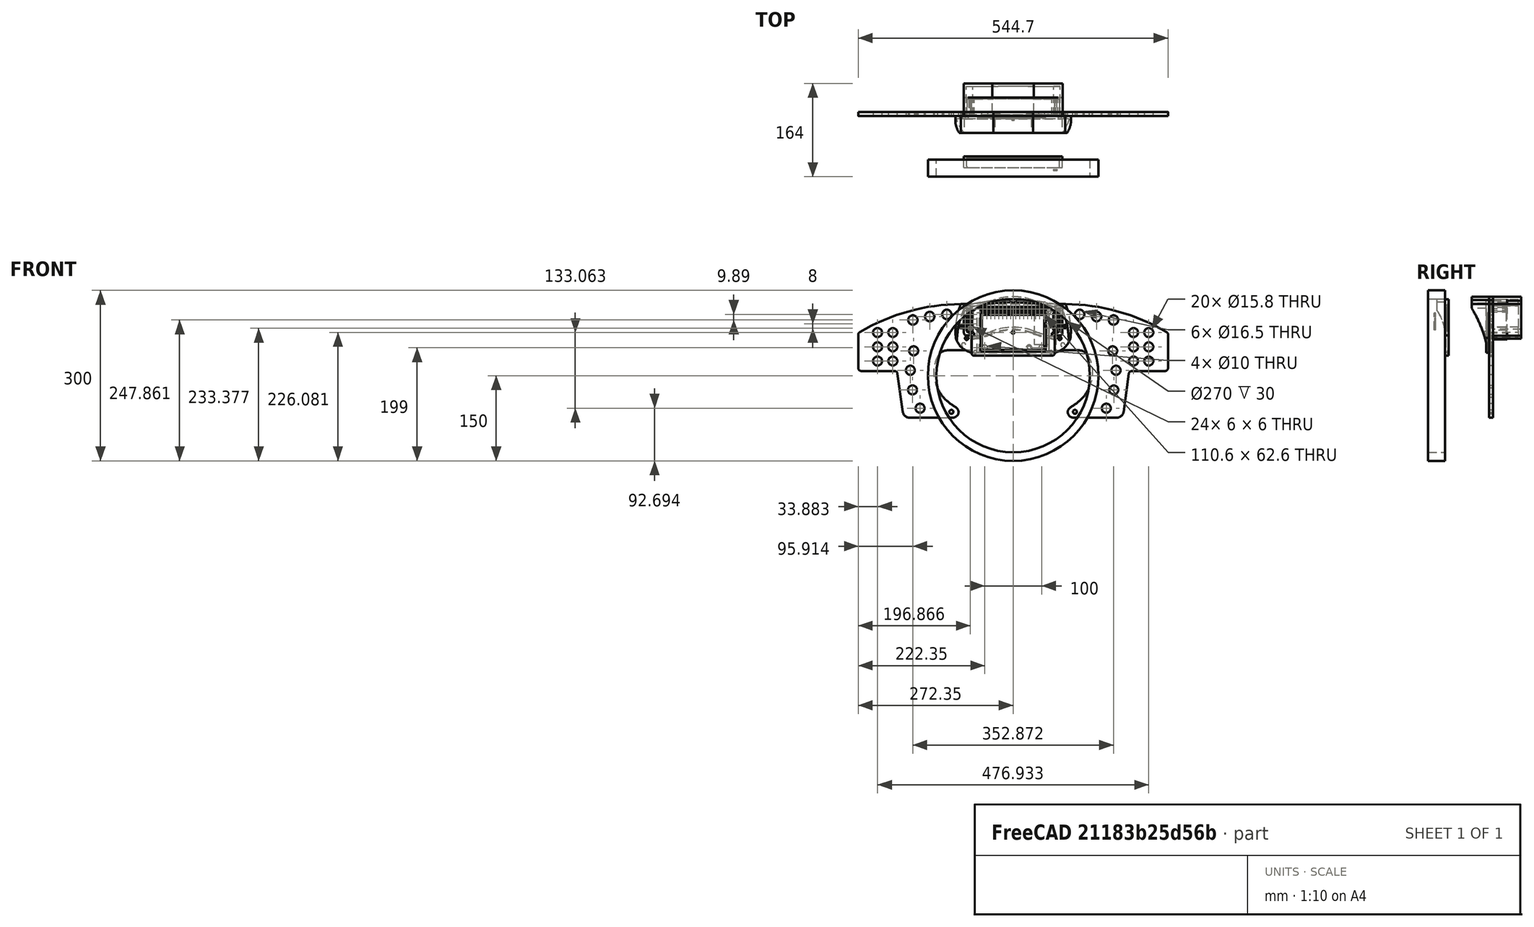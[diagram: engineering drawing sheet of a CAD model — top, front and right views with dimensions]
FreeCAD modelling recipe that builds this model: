
FCSTD DOCUMENT  (FreeCAD 0.20R29177 (Git))
Label: CSW Dashboard V1.1
License: All rights reserved
LicenseURL: http://en.wikipedia.org/wiki/All_rights_reserved
objects: Sketcher::SketchObject×51, PartDesign::Pocket×26, PartDesign::Pad×18, PartDesign::Body×9, PartDesign::Mirrored×3, PartDesign::Chamfer×2, Mesh::Feature×2, Image::ImagePlane×1, Spreadsheet::Sheet×1, Part::FeaturePython×1
note: 156 computed .brp shape members not serialized (recipe doc carries the construction recipe); baked Part::Feature solids carry a one-line shape summary decoded from their .brp

FEATURE [Image::ImagePlane] ImagePlane  label="_CSW_reference"
  Placement = pos=(1.5,53,-30.7) rot=(-1,0,0;4.71239rad)
  XSize = 323.235
  YSize = 168.408
FEATURE [Sketcher::SketchObject] Sketch  label="sk_mount_plate"
  AttachmentOffset = pos=(0,14,0) rot=(0,0,1;0rad)
  FullyConstrained = true
  MapMode = 5
  Placement = pos=(0,-3.1e-15,14) rot=(1,0,0;1.5708rad)
  Support = -> [XZ_Plane002]
  sketch-geometry (13):
    g0: Circle CenterX=-28 CenterY=0 CenterZ=0 NormalX=0 NormalY=0 NormalZ=1 AngleXU=0 Radius=2.425
    g1: Circle CenterX=28 CenterY=0 CenterZ=0 NormalX=0 NormalY=0 NormalZ=1 AngleXU=0 Radius=2.425
    g2: Circle CenterX=-50 CenterY=0 CenterZ=0 NormalX=0 NormalY=0 NormalZ=1 AngleXU=0 Radius=4.85
    g3: Circle CenterX=50 CenterY=0 CenterZ=0 NormalX=0 NormalY=0 NormalZ=1 AngleXU=0 Radius=4.85
    g4: LineSegment StartX=-50 StartY=0 StartZ=0 EndX=50 EndY=0 EndZ=0
    g5: ArcOfCircle CenterX=-5.9e-15 CenterY=-69 CenterZ=0 NormalX=0 NormalY=0 NormalZ=1 AngleXU=0 Radius=100 StartAngle=1.21654 EndAngle=1.92505
    g6: ArcOfCircle CenterX=106.026 CenterY=217.668 CenterZ=0 NormalX=0 NormalY=0 NormalZ=1 AngleXU=0 Radius=205.647 StartAngle=4.35814 EndAngle=4.64413
    g7: GeomPoint X=0 Y=31 Z=0
    g8: LineSegment StartX=28 StartY=0 StartZ=0 EndX=28 EndY=27 EndZ=0
    g9: LineSegment StartX=50 StartY=0 StartZ=0 EndX=50 EndY=19.8 EndZ=0
    g10: ArcOfCircle CenterX=-106.026 CenterY=217.668 CenterZ=0 NormalX=0 NormalY=0 NormalZ=1 AngleXU=0 Radius=205.647 StartAngle=4.78065 EndAngle=5.06664
    g11: LineSegment StartX=-50 StartY=0 StartZ=0 EndX=-50 EndY=19.8 EndZ=0
    g12: LineSegment StartX=-92 StartY=12.5 StartZ=0 EndX=-92 EndY=0 EndZ=0
  constraints (36):
    c: DistanceX(g0,g1) = 56  'mount_holes_distance'
    c: Symmetric(g0,g1,g-2)
    c: Equal(g0,g1)
    c: Diameter(g0) = 4.85  'mount_holes_diameter'
    c: Equal(g2,g3)
    c: Diameter(g2) = 9.7  'motor_mount_holes_diameter'
    c: Symmetric(g2,g3,g-2)
    c: Coincident(g4,g2)
    c: Coincident(g4,g3)
    c: PointOnObject(g0,g4)
    c: PointOnObject(g-1,g4)
    c: Symmetric(g5,g5,g-2)
    c: Coincident(g6,g5)
    c: PointOnObject(g7,g5)
    c: PointOnObject(g7,g-2)
    c: DistanceY(g-1,g7) = 31
    c: Coincident(g8,g1)
    c: PointOnObject(g8,g5)
    c: Vertical(g8)
    c: Coincident(g9,g3)
    c: PointOnObject(g9,g6)
    c: Vertical(g9)
    c: DistanceY(g1,g8) = 27
    c: DistanceX(g2,g3) = 100
    c: DistanceY(g9,g9) = 19.8
    c: Coincident(g11,g2)
    c: PointOnObject(g11,g10)
    c: Vertical(g11)
    c: DistanceY(g11,g11) = 19.8
    c: Symmetric(g6,g10,g-2)
    c: Coincident(g12,g10)
    c: PointOnObject(g12,g-1)
    c: Vertical(g12)
    c: DistanceY(g12,g12) = 12.5
    c: DistanceX(g12,g-1) = 92
    c: Tangent(g10,g5) = 1.5708
FEATURE [Sketcher::SketchObject] Sketch001
  FullyConstrained = true
  MapMode = 5
  Placement = pos=(0,0,0) rot=(1,0,0;1.5708rad)
  Support = -> [XZ_Plane]
FEATURE [Sketcher::SketchObject] Sketch005  label="sk_front_frame"
  FullyConstrained = true
  MapMode = 5
  Placement = pos=(0,0,0) rot=(1,0,0;1.5708rad)
  Support = -> [XZ_Plane002]
  expr: Constraints[17] = <<Spreadsheet>>.case_top_border_radius
  expr: Constraints[18] = <<Spreadsheet>>.case_middle_border_radius
  expr: Constraints[36] = <<Spreadsheet>>.case_top_radius
  expr: Constraints[58] = <<Spreadsheet>>.case_border_thickness
  expr: Constraints[59] = <<Spreadsheet>>.case_border_thickness
  expr: Constraints[60] = <<Spreadsheet>>.case_border_thickness
  expr: Constraints[61] = <<Spreadsheet>>.case_border_thickness
  expr: Constraints[66] = <<Spreadsheet>>.case_border_thickness
  expr: Constraints[67] = <<Spreadsheet>>.case_height
  expr: Constraints[68] = <<Spreadsheet>>.case_width_bottom
  expr: Constraints[69] = <<Spreadsheet>>.case_height_bottom
  expr: Constraints[70] = <<Spreadsheet>>.case_width_top
  sketch-geometry (29):
    g0: LineSegment StartX=73.255 StartY=35.51 StartZ=0 EndX=73.255 EndY=5 EndZ=0
    g1: LineSegment StartX=68.255 StartY=0 StartZ=0 EndX=-68.255 EndY=0 EndZ=0
    g2: LineSegment StartX=-73.255 StartY=5 StartZ=0 EndX=-73.255 EndY=35.51 EndZ=0
    g3: LineSegment StartX=-73.255 StartY=35.51 StartZ=0 EndX=-81.66 EndY=35.51 EndZ=0
    g4: LineSegment StartX=-86.66 StartY=40.51 StartZ=0 EndX=-86.66 EndY=79.3718 EndZ=0
    g5: LineSegment StartX=86.66 StartY=79.3718 StartZ=0 EndX=86.66 EndY=40.51 EndZ=0
    g6: LineSegment StartX=81.66 StartY=35.51 StartZ=0 EndX=73.255 EndY=35.51 EndZ=0
    g7: ArcOfCircle CenterX=-76.66 CenterY=79.3718 CenterZ=0 NormalX=0 NormalY=0 NormalZ=1 AngleXU=0 Radius=10 StartAngle=1.82068 EndAngle=3.14159
    g8: ArcOfCircle CenterX=76.66 CenterY=79.3718 CenterZ=0 NormalX=0 NormalY=0 NormalZ=1 AngleXU=0 Radius=10 StartAngle=-9e-16 EndAngle=1.32091
    g9: ArcOfCircle CenterX=-81.66 CenterY=40.51 CenterZ=0 NormalX=0 NormalY=0 NormalZ=1 AngleXU=0 Radius=5 StartAngle=3.14159 EndAngle=4.71239
    g10: ArcOfCircle CenterX=81.66 CenterY=40.51 CenterZ=0 NormalX=0 NormalY=0 NormalZ=1 AngleXU=0 Radius=5 StartAngle=4.71239 EndAngle=6.28319
    g11: ArcOfCircle CenterX=68.255 CenterY=5 CenterZ=0 NormalX=0 NormalY=0 NormalZ=1 AngleXU=0 Radius=5 StartAngle=4.71239 EndAngle=6.28319
    g12: ArcOfCircle CenterX=-68.255 CenterY=5 CenterZ=0 NormalX=0 NormalY=0 NormalZ=1 AngleXU=0 Radius=5 StartAngle=3.14159 EndAngle=4.71239
    g13: ArcOfCircle CenterX=8.8e-15 CenterY=-221 CenterZ=0 NormalX=0 NormalY=0 NormalZ=1 AngleXU=0 Radius=320 StartAngle=1.32091 EndAngle=1.82068
    g14: LineSegment StartX=81.66 StartY=75.6038 StartZ=0 EndX=81.66 EndY=45.51 EndZ=0
    g15: LineSegment StartX=63.255 StartY=5 StartZ=0 EndX=-63.255 EndY=5 EndZ=0
    g16: LineSegment StartX=-81.66 StartY=45.51 StartZ=0 EndX=-81.66 EndY=75.6038 EndZ=0
    g17: ArcOfCircle CenterX=-71.66 CenterY=75.6038 CenterZ=0 NormalX=0 NormalY=0 NormalZ=1 AngleXU=0 Radius=10 StartAngle=1.80407 EndAngle=3.14159
    g18: ArcOfCircle CenterX=71.66 CenterY=75.6038 CenterZ=0 NormalX=0 NormalY=0 NormalZ=1 AngleXU=0 Radius=10 StartAngle=-9e-16 EndAngle=1.33753
    g19: ArcOfCircle CenterX=-1.33e-14 CenterY=-226 CenterZ=0 NormalX=0 NormalY=0 NormalZ=1 AngleXU=0 Radius=320 StartAngle=1.33753 EndAngle=1.80407
    g20: LineSegment StartX=-76.66 StartY=40.51 StartZ=0 EndX=-68.255 EndY=40.51 EndZ=0
    g21: LineSegment StartX=-68.255 StartY=40.51 StartZ=0 EndX=-68.255 EndY=10 EndZ=0
    g22: LineSegment StartX=76.66 StartY=40.51 StartZ=0 EndX=68.255 EndY=40.51 EndZ=0
    g23: LineSegment StartX=68.255 StartY=40.51 StartZ=0 EndX=68.255 EndY=10 EndZ=0
    g24: ArcOfCircle CenterX=-76.66 CenterY=45.51 CenterZ=0 NormalX=0 NormalY=0 NormalZ=1 AngleXU=0 Radius=5 StartAngle=3.14159 EndAngle=4.71239
    g25: ArcOfCircle CenterX=-63.255 CenterY=10 CenterZ=0 NormalX=0 NormalY=0 NormalZ=1 AngleXU=0 Radius=5 StartAngle=3.14159 EndAngle=4.71239
    g26: ArcOfCircle CenterX=63.255 CenterY=10 CenterZ=0 NormalX=0 NormalY=0 NormalZ=1 AngleXU=0 Radius=5 StartAngle=4.71239 EndAngle=6.28319
    g27: ArcOfCircle CenterX=76.66 CenterY=45.51 CenterZ=0 NormalX=0 NormalY=0 NormalZ=1 AngleXU=0 Radius=5 StartAngle=4.71239 EndAngle=6.28319
    g28: LineSegment StartX=0 StartY=94 StartZ=0 EndX=0 EndY=99 EndZ=0
  constraints (73):
    c: Horizontal(g1)
    c: Vertical(g2)
    c: Vertical(g0)
    c: Horizontal(g3)
    c: Vertical(g5)
    c: Horizontal(g6)
    c: Coincident(g2,g3)
    c: Coincident(g0,g6)
    c: Tangent(g4,g7) = 1.5708
    c: Tangent(g5,g8) = 1.5708
    c: Tangent(g4,g9) = 1.5708
    c: Tangent(g3,g9) = 1.5708
    c: Tangent(g5,g10) = 1.5708
    c: Tangent(g6,g10) = 1.5708
    c: Symmetric(g2,g0,g-2)
    c: Symmetric(g4,g5,g-2)
    c: Equal(g9,g10)
    c: Radius(g7) = 10
    c: Radius(g9) = 5
    c: Tangent(g0,g11) = 1.5708
    c: Tangent(g1,g11) = 1.5708
    c: Tangent(g2,g12) = 1.5708
    c: Tangent(g1,g12) = 1.5708
    c: Equal(g12,g11)
    c: Equal(g11,g9)
    c: Tangent(g13,g7) = -1.5708
    c: Tangent(g13,g8) = -1.5708
    c: Horizontal(g15)
    c: Vertical(g14)
    c: Vertical(g16)
    c: Tangent(g16,g17) = 1.5708
    c: Tangent(g14,g18) = 1.5708
    c: Equal(g17,g18)
    c: Equal(g18,g7)
    c: Tangent(g19,g17) = -1.5708
    c: Tangent(g19,g18) = -1.5708
    c: Radius(g13) = 320
    c: Horizontal(g20)
    c: Coincident(g21,g20)
    c: Vertical(g21)
    c: Coincident(g23,g22)
    c: Vertical(g23)
    c: Horizontal(g22)
    c: Tangent(g16,g24) = 1.5708
    c: Tangent(g20,g24) = -1.5708
    c: Tangent(g21,g25) = -1.5708
    c: Tangent(g15,g25) = 1.5708
    c: Tangent(g23,g26) = 1.5708
    c: Tangent(g15,g26) = 1.5708
    c: Tangent(g14,g27) = 1.5708
    c: Tangent(g22,g27) = 1.5708
    c: Equal(g9,g24)
    c: Equal(g24,g25)
    c: Equal(g25,g26)
    c: Equal(g26,g27)
    c: Symmetric(g20,g22,g-2)
    c: Symmetric(g16,g14,g-2)
    c: Equal(g13,g19)
    c: DistanceX(g2,g21) = 5
    c: DistanceY(g1,g15) = 5
    c: DistanceY(g2,g20) = 5
    c: DistanceX(g4,g16) = 5
    c: PointOnObject(g28,g19)
    c: PointOnObject(g28,g13)
    c: Vertical(g28)
    c: PointOnObject(g28,g-2)
    c: DistanceY(g28,g28) = 5
    c: DistanceY(g1,g28) = 99
    c: DistanceX(g2,g0) = 146.51
    c: DistanceY(g1,g0) = 35.51
    c: DistanceX(g4,g5) = 173.32
    c: Symmetric(g7,g8,g-2)
    c: PointOnObject(g1,g-1)
FEATURE [Spreadsheet::Sheet] Spreadsheet
  cells = A2=display_width; B2(display_width)=119.3; A3=display_height; B3(display_height)=68.7; A4=display_depth; B4(display_depth)=3.6; A5=screen_width; B5(screen_width)=109.6; A6=screen_height; B6(screen_height)=61.6; A7=screen_offset_left; B7(screen_offset_left)=8; A10=case_top_border_radius; B10(case_top_border_radius)=10; A11=case_middle_border_radius; B11(case_middle_border_radius)=5; A12=case_border_thickness; B12(case_border_thickness)=5; A15=case_height; B15(case_height)=99; A16=case_width_top; B16(case_width_top)=173.32; A17=case_width_bottom; B17(case_width_bottom)=146.51; A18=case_height_bottom; B18(case_height_bottom)=35.51; A19=case_top_radius; B19(case_top_radius)=320; A22=ref_leds_gap; B22(ref_leds_gap)=1.4; A23=ref_leds_width; B23(ref_leds_width)=6
FEATURE [Sketcher::SketchObject] Sketch007  label="sk_front_back_display_cutout"
  AttachmentOffset = pos=(0,41,10) rot=(0,0,1;0rad)
  FullyConstrained = true
  MapMode = 5
  Placement = pos=(0,-10,41) rot=(1,0,0;1.5708rad)
  Support = -> [XZ_Plane002]
  expr: Constraints[8] = <<Spreadsheet>>.display_width + 1
  expr: Constraints[9] = <<Spreadsheet>>.display_height + 1
  sketch-geometry (4):
    g0: LineSegment StartX=-63.19 StartY=34.77 StartZ=0 EndX=57.11 EndY=34.77 EndZ=0
    g1: LineSegment StartX=57.11 StartY=34.77 StartZ=0 EndX=57.11 EndY=-34.93 EndZ=0
    g2: LineSegment StartX=57.11 StartY=-34.93 StartZ=0 EndX=-63.19 EndY=-34.93 EndZ=0
    g3: LineSegment StartX=-63.19 StartY=-34.93 StartZ=0 EndX=-63.19 EndY=34.77 EndZ=0
  constraints (12):
    c: Coincident(g0,g1)
    c: Coincident(g1,g2)
    c: Coincident(g2,g3)
    c: Coincident(g3,g0)
    c: Horizontal(g0)
    c: Horizontal(g2)
    c: Vertical(g1)
    c: Vertical(g3)
    c: DistanceX(g0,g0) = 120.3
    c: DistanceY(g1,g1) = 69.7
    c: DistanceX(g0,g-1) = 63.19
    c: DistanceY(g-1,g0) = 34.77
FEATURE [PartDesign::Pad] Pad005  label="front_main_frame"
  Direction = (0,-1,-2e-16)
  Length = 20
  Length2 = 10
  Midplane = true
  Placement = pos=(0,0,0) rot=(1,0,0;1.5708rad)
  Profile = -> Sketch005
  ReferenceAxis = -> Sketch005 [N_Axis]
  Refine = true
  Type = 0
FEATURE [Sketcher::SketchObject] Sketch008  label="sk_front_screen_frame"
  AttachmentOffset = pos=(0,0,4) rot=(0,0,1;0rad)
  ExternalGeometry = -> [Sketch005]
  FullyConstrained = false
  MapMode = 5
  Placement = pos=(0,-4,-9e-16) rot=(1,0,0;1.5708rad)
  Support = -> [XZ_Plane002]
  expr: Constraints[37] = <<Spreadsheet>>.screen_width + 1
  expr: Constraints[38] = <<Spreadsheet>>.screen_height + 1
  sketch-geometry (18):
    g0: LineSegment StartX=86.66 StartY=79.3718 StartZ=0 EndX=86.66 EndY=40.51 EndZ=0
    g1: LineSegment StartX=68.255 StartY=0 StartZ=0 EndX=-68.255 EndY=0 EndZ=0
    g2: LineSegment StartX=-86.66 StartY=40.51 StartZ=0 EndX=-86.66 EndY=79.3718 EndZ=0
    g3: LineSegment StartX=-81.66 StartY=35.51 StartZ=0 EndX=-73.255 EndY=35.51 EndZ=0
    g4: LineSegment StartX=-73.255 StartY=35.51 StartZ=0 EndX=-73.255 EndY=5 EndZ=0
    g5: LineSegment StartX=81.66 StartY=35.51 StartZ=0 EndX=73.255 EndY=35.51 EndZ=0
    g6: LineSegment StartX=73.255 StartY=35.51 StartZ=0 EndX=73.255 EndY=5 EndZ=0
    g7: ArcOfCircle CenterX=-76.66 CenterY=79.3718 CenterZ=0 NormalX=0 NormalY=0 NormalZ=1 AngleXU=0 Radius=10 StartAngle=1.82068 EndAngle=3.14159
    g8: ArcOfCircle CenterX=-81.66 CenterY=40.51 CenterZ=0 NormalX=0 NormalY=0 NormalZ=1 AngleXU=0 Radius=5 StartAngle=3.14159 EndAngle=4.71239
    g9: ArcOfCircle CenterX=-68.255 CenterY=5 CenterZ=0 NormalX=0 NormalY=0 NormalZ=1 AngleXU=0 Radius=5 StartAngle=3.14159 EndAngle=4.71239
    g10: ArcOfCircle CenterX=68.255 CenterY=5 CenterZ=0 NormalX=0 NormalY=0 NormalZ=1 AngleXU=0 Radius=5 StartAngle=4.71239 EndAngle=6.28319
    g11: ArcOfCircle CenterX=81.66 CenterY=40.51 CenterZ=0 NormalX=0 NormalY=0 NormalZ=1 AngleXU=0 Radius=5 StartAngle=4.71239 EndAngle=6.28319
    g12: ArcOfCircle CenterX=76.66 CenterY=79.3718 CenterZ=0 NormalX=0 NormalY=0 NormalZ=1 AngleXU=0 Radius=10 StartAngle=2.598e-13 EndAngle=1.32091
    g13: ArcOfCircle CenterX=-6.18e-14 CenterY=-221 CenterZ=0 NormalX=0 NormalY=0 NormalZ=1 AngleXU=0 Radius=320 StartAngle=1.32091 EndAngle=1.82068
    g14: LineSegment StartX=-55.3 StartY=72.381 StartZ=0 EndX=55.3 EndY=72.381 EndZ=0
    g15: LineSegment StartX=55.3 StartY=72.381 StartZ=0 EndX=55.3 EndY=9.781 EndZ=0
    g16: LineSegment StartX=55.3 StartY=9.781 StartZ=0 EndX=-55.3 EndY=9.781 EndZ=0
    g17: LineSegment StartX=-55.3 StartY=9.781 StartZ=0 EndX=-55.3 EndY=72.381 EndZ=0
  constraints (39):
    c: Horizontal(g1)
    c: Horizontal(g3)
    c: Coincident(g4,g3)
    c: Vertical(g4)
    c: Coincident(g6,g5)
    c: Horizontal(g5)
    c: Tangent(g2,g8) = 1.5708
    c: Tangent(g3,g8) = -1.5708
    c: Tangent(g4,g9) = -1.5708
    c: Tangent(g1,g9) = 1.5708
    c: Tangent(g6,g10) = 1.5708
    c: Tangent(g1,g10) = 1.5708
    c: Tangent(g5,g11) = 1.5708
    c: Tangent(g0,g11) = 1.5708
    c: Symmetric(g4,g6,g-2)
    c: Symmetric(g3,g5,g-2)
    c: Symmetric(g2,g0,g-2)
    c: Tangent(g13,g7) = -1.5708
    c: Tangent(g12,g13) = -1.5708
    c: Coincident(g2,g-6)
    c: Coincident(g3,g-8)
    c: Coincident(g1,g-10)
    c: Coincident(g7,g-4)
    c: Coincident(g12,g-16)
    c: Equal(g13,g-3)
    c: Coincident(g2,g-5)
    c: Coincident(g7,g2)
    c: Coincident(g12,g0)
    c: Coincident(g0,g-15)
    c: Coincident(g14,g15)
    c: Coincident(g15,g16)
    c: Coincident(g16,g17)
    c: Coincident(g17,g14)
    c: Horizontal(g16)
    c: Vertical(g15)
    c: Vertical(g17)
    c: Symmetric(g14,g14,g-2)
    c: DistanceX(g14,g14) = 110.6
    c: DistanceY(g15,g15) = 62.6
FEATURE [PartDesign::Pad] Pad006  label="front_screen_frame"
  BaseFeature = -> Pad005
  Direction = (0,-1,-2e-16)
  Length = 6
  Length2 = 10
  Placement = pos=(0,0,0) rot=(1,0,0;1.5708rad)
  Profile = -> Sketch008
  ReferenceAxis = -> Sketch008 [N_Axis]
  Refine = true
  Type = 0
FEATURE [PartDesign::Pocket] Pocket  label="front_back_display_cutout"
  BaseFeature = -> Pad006
  Direction = (0,1,2e-16)
  Length = 5
  Length2 = 5
  Placement = pos=(0,0,0) rot=(1,0,0;1.5708rad)
  Profile = -> Sketch007
  ReferenceAxis = -> Sketch007 [N_Axis]
  Refine = true
  Type = 0
FEATURE [Sketcher::SketchObject] Sketch009  label="sk_front_side_cutout"
  AttachmentOffset = pos=(0,0,87) rot=(0,0,1;0rad)
  ExternalGeometry = -> [Pocket]
  FullyConstrained = true
  MapMode = 5
  Placement = pos=(87,-1.93e-14,1.93e-14) rot=(0.57735,0.57735,0.57735;2.0944rad)
  Support = -> [YZ_Plane002]
  sketch-geometry (4):
    g0: LineSegment StartX=10 StartY=-1.42e-14 StartZ=0 EndX=-4 EndY=-1.42e-14 EndZ=0
    g1: LineSegment StartX=-4 StartY=-1.42e-14 StartZ=0 EndX=-4 EndY=35.51 EndZ=0
    g2: LineSegment StartX=10 StartY=79.3718 StartZ=0 EndX=10 EndY=-1.42e-14 EndZ=0
    g3: ArcOfCircle CenterX=71.7093 CenterY=35.51 CenterZ=0 NormalX=0 NormalY=0 NormalZ=1 AngleXU=0 Radius=75.7093 StartAngle=2.52367 EndAngle=3.14159
  constraints (10):
    c: Coincident(g0,g1)
    c: Coincident(g2,g0)
    c: Horizontal(g0)
    c: Vertical(g1)
    c: Coincident(g0,g-6)
    c: Distance(g-6,g0) = 6
    c: Coincident(g3,g-4)
    c: Tangent(g3,g1) = 1.5708
    c: Coincident(g2,g3)
    c: PointOnObject(g1,g-5)
FEATURE [PartDesign::Pocket] Pocket001  label="front_side_cutout"
  BaseFeature = -> Pocket
  Direction = (-1,2e-16,-3e-16)
  Length = 5
  Length2 = 5
  Placement = pos=(0,0,0) rot=(1,0,0;1.5708rad)
  Profile = -> Sketch009
  ReferenceAxis = -> Sketch009 [N_Axis]
  Refine = true
  Type = 1
FEATURE [Sketcher::SketchObject] Sketch010  label="sk_mount_plate001"
  AttachmentOffset = pos=(0,14,0) rot=(0,0,1;0rad)
  FullyConstrained = true
  MapMode = 5
  Placement = pos=(0,-3.1e-15,14) rot=(1,0,0;1.5708rad)
  Support = -> [XZ_Plane]
  sketch-geometry (14):
    g0: Circle CenterX=-28 CenterY=0 CenterZ=0 NormalX=0 NormalY=0 NormalZ=1 AngleXU=0 Radius=3
    g1: Circle CenterX=28 CenterY=0 CenterZ=0 NormalX=0 NormalY=0 NormalZ=1 AngleXU=0 Radius=3
    g2: Circle CenterX=-50 CenterY=0 CenterZ=0 NormalX=0 NormalY=0 NormalZ=1 AngleXU=0 Radius=5
    g3: Circle CenterX=50 CenterY=0 CenterZ=0 NormalX=0 NormalY=0 NormalZ=1 AngleXU=0 Radius=5
    g4: LineSegment StartX=-50 StartY=0 StartZ=0 EndX=50 EndY=0 EndZ=0
    g5: ArcOfCircle CenterX=1.69e-14 CenterY=-69 CenterZ=0 NormalX=0 NormalY=0 NormalZ=1 AngleXU=0 Radius=100 StartAngle=1.21654 EndAngle=1.92505
    g6: ArcOfCircle CenterX=106.026 CenterY=217.668 CenterZ=0 NormalX=0 NormalY=0 NormalZ=1 AngleXU=0 Radius=205.647 StartAngle=4.35814 EndAngle=4.64413
    g7: GeomPoint X=0 Y=31 Z=0
    g8: LineSegment StartX=28 StartY=0 StartZ=0 EndX=28 EndY=27 EndZ=0
    g9: LineSegment StartX=50 StartY=0 StartZ=0 EndX=50 EndY=19.8 EndZ=0
    g10: ArcOfCircle CenterX=-106.026 CenterY=217.668 CenterZ=0 NormalX=0 NormalY=0 NormalZ=1 AngleXU=0 Radius=205.647 StartAngle=4.78065 EndAngle=5.06664
    g11: LineSegment StartX=-50 StartY=0 StartZ=0 EndX=-50 EndY=19.8 EndZ=0
    g12: LineSegment StartX=-92 StartY=12.5 StartZ=0 EndX=-92 EndY=0 EndZ=0
    g13: LineSegment StartX=92 StartY=12.5 StartZ=0 EndX=92 EndY=0 EndZ=0
  constraints (39):
    c: DistanceX(g0,g1) = 56  'mount_holes_distance'
    c: Symmetric(g0,g1,g-2)
    c: Equal(g0,g1)
    c: Diameter(g0) = 6  'mount_holes_diameter'
    c: Equal(g2,g3)
    c: Diameter(g2) = 10  'motor_mount_holes_diameter'
    c: Symmetric(g2,g3,g-2)
    c: Coincident(g4,g2)
    c: Coincident(g4,g3)
    c: PointOnObject(g0,g4)
    c: PointOnObject(g-1,g4)
    c: Symmetric(g5,g5,g-2)
    c: Coincident(g6,g5)
    c: PointOnObject(g7,g5)
    c: PointOnObject(g7,g-2)
    c: DistanceY(g-1,g7) = 31
    c: Coincident(g8,g1)
    c: PointOnObject(g8,g5)
    c: Vertical(g8)
    c: Coincident(g9,g3)
    c: PointOnObject(g9,g6)
    c: Vertical(g9)
    c: DistanceY(g1,g8) = 27
    c: DistanceX(g2,g3) = 100
    c: DistanceY(g9,g9) = 19.8
    c: Coincident(g11,g2)
    c: PointOnObject(g11,g10)
    c: Vertical(g11)
    c: DistanceY(g11,g11) = 19.8
    c: Symmetric(g6,g10,g-2)
    c: Coincident(g12,g10)
    c: PointOnObject(g12,g-1)
    c: Vertical(g12)
    c: DistanceY(g12,g12) = 12.5
    c: DistanceX(g12,g-1) = 92
    c: Tangent(g10,g5) = 1.5708
    c: Coincident(g13,g6)
    c: PointOnObject(g13,g-1)
    c: Vertical(g13)
FEATURE [Sketcher::SketchObject] Sketch011  label="sk_back_plate"
  FullyConstrained = false
  MapMode = 5
  Placement = pos=(0,0,0) rot=(1,0,0;1.5708rad)
  Support = -> [XZ_Plane]
  expr: Constraints[16] = <<Spreadsheet>>.case_top_border_radius
  expr: Constraints[17] = <<Spreadsheet>>.case_middle_border_radius
  expr: Constraints[26] = <<Spreadsheet>>.case_top_radius
  expr: Constraints[30] = <<Spreadsheet>>.case_border_thickness
  expr: Constraints[31] = <<Spreadsheet>>.case_height
  expr: Constraints[32] = <<Spreadsheet>>.case_width_bottom
  expr: Constraints[33] = <<Spreadsheet>>.case_height_bottom
  expr: Constraints[34] = <<Spreadsheet>>.case_width_top
  sketch-geometry (15):
    g0: LineSegment StartX=73.255 StartY=35.51 StartZ=0 EndX=73.255 EndY=5 EndZ=0
    g1: LineSegment StartX=68.255 StartY=0 StartZ=0 EndX=-68.255 EndY=0 EndZ=0
    g2: LineSegment StartX=-73.255 StartY=5 StartZ=0 EndX=-73.255 EndY=35.51 EndZ=0
    g3: LineSegment StartX=-73.255 StartY=35.51 StartZ=0 EndX=-81.66 EndY=35.51 EndZ=0
    g4: LineSegment StartX=-86.66 StartY=40.51 StartZ=0 EndX=-86.66 EndY=79.3718 EndZ=0
    g5: LineSegment StartX=86.66 StartY=79.3718 StartZ=0 EndX=86.66 EndY=40.51 EndZ=0
    g6: LineSegment StartX=81.66 StartY=35.51 StartZ=0 EndX=73.255 EndY=35.51 EndZ=0
    g7: ArcOfCircle CenterX=-76.66 CenterY=79.3718 CenterZ=0 NormalX=0 NormalY=0 NormalZ=1 AngleXU=0 Radius=10 StartAngle=1.82068 EndAngle=3.14159
    g8: ArcOfCircle CenterX=76.66 CenterY=79.3718 CenterZ=0 NormalX=0 NormalY=0 NormalZ=1 AngleXU=0 Radius=10 StartAngle=-6.2e-15 EndAngle=1.32091
    g9: ArcOfCircle CenterX=-81.66 CenterY=40.51 CenterZ=0 NormalX=0 NormalY=0 NormalZ=1 AngleXU=0 Radius=5 StartAngle=3.14159 EndAngle=4.71239
    g10: ArcOfCircle CenterX=81.66 CenterY=40.51 CenterZ=0 NormalX=0 NormalY=0 NormalZ=1 AngleXU=0 Radius=5 StartAngle=4.71239 EndAngle=6.28319
    g11: ArcOfCircle CenterX=68.255 CenterY=5 CenterZ=0 NormalX=0 NormalY=0 NormalZ=1 AngleXU=0 Radius=5 StartAngle=4.71239 EndAngle=6.28319
    g12: ArcOfCircle CenterX=-68.255 CenterY=5 CenterZ=0 NormalX=0 NormalY=0 NormalZ=1 AngleXU=0 Radius=5 StartAngle=3.14159 EndAngle=4.71239
    g13: ArcOfCircle CenterX=8.8e-15 CenterY=-221 CenterZ=0 NormalX=0 NormalY=0 NormalZ=1 AngleXU=0 Radius=320 StartAngle=1.32091 EndAngle=1.82068
    g14: LineSegment StartX=0 StartY=94 StartZ=0 EndX=0 EndY=99 EndZ=0
  constraints (39):
    c: Horizontal(g1)
    c: Vertical(g2)
    c: Vertical(g0)
    c: Horizontal(g3)
    c: Vertical(g5)
    c: Horizontal(g6)
    c: Coincident(g2,g3)
    c: Coincident(g0,g6)
    c: Tangent(g4,g7) = 1.5708
    c: Tangent(g4,g9) = 1.5708
    c: Tangent(g3,g9) = 1.5708
    c: Tangent(g5,g10) = 1.5708
    c: Tangent(g6,g10) = 1.5708
    c: Symmetric(g2,g0,g-2)
    c: Symmetric(g4,g5,g-2)
    c: Equal(g9,g10)
    c: Radius(g7) = 10
    c: Radius(g9) = 5
    c: Tangent(g0,g11) = 1.5708
    c: Tangent(g1,g11) = 1.5708
    c: Tangent(g2,g12) = 1.5708
    c: Tangent(g1,g12) = 1.5708
    c: Equal(g12,g11)
    c: Equal(g11,g9)
    c: Tangent(g13,g7) = -1.5708
    c: Tangent(g13,g8) = -1.5708
    c: Radius(g13) = 320
    c: PointOnObject(g14,g13)
    c: Vertical(g14)
    c: PointOnObject(g14,g-2)
    c: DistanceY(g14,g14) = 5
    c: DistanceY(g1,g14) = 99
    c: DistanceX(g2,g0) = 146.51
    c: DistanceY(g1,g0) = 35.51
    c: DistanceX(g4,g5) = 173.32
    c: Symmetric(g7,g8,g-2)
    c: PointOnObject(g1,g-1)
    c: Vertical(g4)
    c: Equal(g8,g7)
FEATURE [PartDesign::Pad] Pad  label="back_plate"
  Direction = (0,-1,-2e-16)
  Length = 7
  Length2 = 10
  Placement = pos=(0,0,0) rot=(1,0,0;1.5708rad)
  Profile = -> Sketch011
  ReferenceAxis = -> Sketch011 [N_Axis]
  Refine = true
  Type = 0
FEATURE [Sketcher::SketchObject] Sketch012  label="sk_backside"
  ExternalGeometry = -> [Sketch011,Sketch010]
  FullyConstrained = true
  MapMode = 5
  Placement = pos=(0,0,0) rot=(1,0,0;1.5708rad)
  Support = -> [XZ_Plane]
  sketch-geometry (14):
    g0: ArcOfCircle CenterX=-2.19e-14 CenterY=-221 CenterZ=0 NormalX=0 NormalY=0 NormalZ=1 AngleXU=0 Radius=320 StartAngle=1.32091 EndAngle=1.82068
    g1: ArcOfCircle CenterX=-76.66 CenterY=79.3718 CenterZ=0 NormalX=0 NormalY=0 NormalZ=1 AngleXU=0 Radius=10 StartAngle=1.82068 EndAngle=3.14159
    g2: ArcOfCircle CenterX=76.66 CenterY=79.3718 CenterZ=0 NormalX=0 NormalY=0 NormalZ=1 AngleXU=0 Radius=10 StartAngle=5e-16 EndAngle=1.32091
    g3: LineSegment StartX=-86.66 StartY=79.3718 StartZ=0 EndX=-86.66 EndY=40.51 EndZ=0
    g4: ArcOfCircle CenterX=-81.66 CenterY=40.51 CenterZ=0 NormalX=0 NormalY=0 NormalZ=1 AngleXU=0 Radius=5 StartAngle=3.14159 EndAngle=4.71239
    g5: LineSegment StartX=-81.66 StartY=35.51 StartZ=0 EndX=-73.255 EndY=35.51 EndZ=0
    g6: ArcOfCircle CenterX=-106.026 CenterY=231.668 CenterZ=0 NormalX=0 NormalY=0 NormalZ=1 AngleXU=0 Radius=205.647 StartAngle=4.87243 EndAngle=5.06664
    g7: ArcOfCircle CenterX=3.4e-15 CenterY=-55 CenterZ=0 NormalX=0 NormalY=0 NormalZ=1 AngleXU=0 Radius=100 StartAngle=1.21654 EndAngle=1.92505
    g8: LineSegment StartX=73.255 StartY=35.51 StartZ=0 EndX=81.66 EndY=35.51 EndZ=0
    g9: ArcOfCircle CenterX=81.66 CenterY=40.51 CenterZ=0 NormalX=0 NormalY=0 NormalZ=1 AngleXU=0 Radius=5 StartAngle=4.71239 EndAngle=6.28319
    g10: LineSegment StartX=86.66 StartY=40.51 StartZ=0 EndX=86.66 EndY=79.3718 EndZ=0
    g11: LineSegment StartX=-73.255 StartY=35.51 StartZ=0 EndX=-73.255 EndY=28.649 EndZ=0
    g12: LineSegment StartX=73.255 StartY=35.51 StartZ=0 EndX=73.255 EndY=28.649 EndZ=0
    g13: ArcOfCircle CenterX=106.026 CenterY=231.668 CenterZ=0 NormalX=0 NormalY=0 NormalZ=1 AngleXU=0 Radius=205.647 StartAngle=4.35814 EndAngle=4.55235
  constraints (34):
    c: Coincident(g0,g-4)
    c: Coincident(g0,g-6)
    c: Coincident(g1,g-5)
    c: Coincident(g1,g0)
    c: Coincident(g2,g0)
    c: Coincident(g2,g-7)
    c: Equal(g0,g-3)
    c: Equal(g1,g-4)
    c: Equal(g2,g-6)
    c: Tangent(g1,g3) = -1.5708
    c: Tangent(g3,g4) = -1.5708
    c: Coincident(g4,g-9)
    c: Tangent(g4,g5) = -1.5708
    c: Coincident(g6,g-13)
    c: Tangent(g6,g7) = 1.5708
    c: Coincident(g7,g-14)
    c: Coincident(g8,g-11)
    c: Tangent(g8,g9) = -1.5708
    c: Coincident(g9,g-10)
    c: Tangent(g9,g10) = -1.5708
    c: Equal(g6,g-12)
    c: Coincident(g5,g-9)
    c: Coincident(g11,g5)
    c: PointOnObject(g11,g-12)
    c: Vertical(g11)
    c: Coincident(g12,g8)
    c: PointOnObject(g12,g-14)
    c: Vertical(g12)
    c: Coincident(g10,g2)
    c: Coincident(g6,g11)
    c: Coincident(g13,g7)
    c: Coincident(g13,g12)
    c: Equal(g13,g-14)
    c: PointOnObject(g12,g-16)
FEATURE [Sketcher::SketchObject] Sketch013  label="sk_mount_cutout"
  ExternalGeometry = -> [Sketch010]
  FullyConstrained = true
  MapMode = 5
  Placement = pos=(0,0,0) rot=(1,0,0;1.5708rad)
  Support = -> [XZ_Plane]
  sketch-geometry (4):
    g0: Circle CenterX=-50 CenterY=14 CenterZ=0 NormalX=0 NormalY=0 NormalZ=1 AngleXU=0 Radius=5
    g1: Circle CenterX=-28 CenterY=14 CenterZ=0 NormalX=0 NormalY=0 NormalZ=1 AngleXU=0 Radius=3
    g2: Circle CenterX=28 CenterY=14 CenterZ=0 NormalX=0 NormalY=0 NormalZ=1 AngleXU=0 Radius=3
    g3: Circle CenterX=50 CenterY=14 CenterZ=0 NormalX=0 NormalY=0 NormalZ=1 AngleXU=0 Radius=5
  constraints (8):
    c: Coincident(g0,g-3)
    c: Coincident(g1,g-4)
    c: Coincident(g2,g-5)
    c: Coincident(g3,g-6)
    c: Equal(g0,g3)
    c: Equal(g3,g-3)
    c: Equal(g1,g-4)
    c: Equal(g-4,g2)
FEATURE [Sketcher::SketchObject] Sketch014  label="sk_frame_cutout_temp"
  AttachmentOffset = pos=(0,0,5) rot=(0,0,1;0rad)
  ExternalGeometry = -> [Sketch011]
  FullyConstrained = false
  MapMode = 5
  Placement = pos=(0,-5,-1.1e-15) rot=(1,0,0;1.5708rad)
  Support = -> [XZ_Plane]
  expr: Constraints[28] = <<Spreadsheet>>.case_border_thickness
  expr: Constraints[29] = <<Spreadsheet>>.case_border_thickness
  expr: Constraints[30] = <<Spreadsheet>>.case_border_thickness
  expr: Constraints[31] = <<Spreadsheet>>.case_border_thickness
  sketch-geometry (15):
    g0: LineSegment StartX=81.66 StartY=75.6038 StartZ=0 EndX=81.66 EndY=45.51 EndZ=0
    g1: LineSegment StartX=63.255 StartY=22.7713 StartZ=0 EndX=-63.255 EndY=22.7713 EndZ=0
    g2: LineSegment StartX=-81.66 StartY=45.51 StartZ=0 EndX=-81.66 EndY=75.6038 EndZ=0
    g3: ArcOfCircle CenterX=-71.66 CenterY=75.6038 CenterZ=0 NormalX=0 NormalY=0 NormalZ=1 AngleXU=0 Radius=10 StartAngle=1.80407 EndAngle=3.14159
    g4: ArcOfCircle CenterX=71.66 CenterY=75.6038 CenterZ=0 NormalX=0 NormalY=0 NormalZ=1 AngleXU=0 Radius=10 StartAngle=-9e-16 EndAngle=1.33753
    g5: ArcOfCircle CenterX=1.51e-14 CenterY=-226 CenterZ=0 NormalX=0 NormalY=0 NormalZ=1 AngleXU=0 Radius=320 StartAngle=1.33753 EndAngle=1.80407
    g6: LineSegment StartX=-76.66 StartY=40.51 StartZ=0 EndX=-68.255 EndY=40.51 EndZ=0
    g7: LineSegment StartX=-68.255 StartY=40.51 StartZ=0 EndX=-68.255 EndY=27.7713 EndZ=0
    g8: LineSegment StartX=76.66 StartY=40.51 StartZ=0 EndX=68.255 EndY=40.51 EndZ=0
    g9: LineSegment StartX=68.255 StartY=40.51 StartZ=0 EndX=68.255 EndY=27.7713 EndZ=0
    g10: ArcOfCircle CenterX=-76.66 CenterY=45.51 CenterZ=0 NormalX=0 NormalY=0 NormalZ=1 AngleXU=0 Radius=5 StartAngle=3.14159 EndAngle=4.71239
    g11: ArcOfCircle CenterX=-63.255 CenterY=27.7713 CenterZ=0 NormalX=0 NormalY=0 NormalZ=1 AngleXU=0 Radius=5 StartAngle=3.14159 EndAngle=4.71239
    g12: ArcOfCircle CenterX=63.255 CenterY=27.7713 CenterZ=0 NormalX=0 NormalY=0 NormalZ=1 AngleXU=0 Radius=5 StartAngle=4.71239 EndAngle=6.28319
    g13: ArcOfCircle CenterX=76.66 CenterY=45.51 CenterZ=0 NormalX=0 NormalY=0 NormalZ=1 AngleXU=0 Radius=5 StartAngle=4.71239 EndAngle=6.28319
    g14: LineSegment StartX=0 StartY=94 StartZ=0 EndX=0 EndY=99 EndZ=0
  constraints (37):
    c: Horizontal(g1)
    c: Vertical(g0)
    c: Tangent(g2,g3) = 1.5708
    c: Tangent(g0,g4) = 1.5708
    c: Tangent(g5,g3) = -1.5708
    c: Tangent(g5,g4) = -1.5708
    c: Horizontal(g6)
    c: Coincident(g7,g6)
    c: Vertical(g7)
    c: Coincident(g9,g8)
    c: Vertical(g9)
    c: Horizontal(g8)
    c: Tangent(g2,g10) = 1.5708
    c: Tangent(g6,g10) = -1.5708
    c: Tangent(g7,g11) = -1.5708
    c: Tangent(g1,g11) = 1.5708
    c: Tangent(g9,g12) = 1.5708
    c: Tangent(g1,g12) = 1.5708
    c: Tangent(g0,g13) = 1.5708
    c: Tangent(g8,g13) = 1.5708
    c: Equal(g10,g11)
    c: Equal(g11,g12)
    c: Equal(g12,g13)
    c: Symmetric(g6,g8,g-2)
    c: Symmetric(g2,g0,g-2)
    c: PointOnObject(g14,g5)
    c: Vertical(g14)
    c: PointOnObject(g14,g-2)
    c: DistanceY(g14,g14) = 5
    c: DistanceX(g-5,g2) = 5
    c: DistanceX(g-9,g7) = 5
    c: DistanceY(g-8,g6) = 5
    c: Equal(g10,g-6)
    c: Equal(g3,g-4)
    c: Equal(g5,g-3)
    c: PointOnObject(g14,g-3)
    c: Symmetric(g3,g4,g-2)
FEATURE [Sketcher::SketchObject] Sketch015  label="sk_frame_cutout"
  AttachmentOffset = pos=(0,0,7) rot=(0,0,1;0rad)
  ExternalGeometry = -> [Sketch014,Sketch010]
  FullyConstrained = true
  MapMode = 5
  Placement = pos=(0,-7,-1.6e-15) rot=(1,0,0;1.5708rad)
  Support = -> [XZ_Plane]
  expr: Constraints[33] = <<Spreadsheet>>.case_border_thickness
  expr: Constraints[38] = <<Spreadsheet>>.case_border_thickness
  sketch-geometry (17):
    g0: LineSegment StartX=81.66 StartY=75.6038 StartZ=0 EndX=81.66 EndY=45.51 EndZ=0
    g1: LineSegment StartX=-81.66 StartY=45.51 StartZ=0 EndX=-81.66 EndY=75.6038 EndZ=0
    g2: ArcOfCircle CenterX=71.66 CenterY=75.6038 CenterZ=0 NormalX=0 NormalY=0 NormalZ=1 AngleXU=0 Radius=10 StartAngle=0 EndAngle=1.33753
    g3: ArcOfCircle CenterX=-71.66 CenterY=75.6038 CenterZ=0 NormalX=0 NormalY=0 NormalZ=1 AngleXU=0 Radius=10 StartAngle=1.80407 EndAngle=3.14159
    g4: ArcOfCircle CenterX=-5.08e-14 CenterY=-226 CenterZ=0 NormalX=0 NormalY=0 NormalZ=1 AngleXU=0 Radius=320 StartAngle=1.33753 EndAngle=1.80407
    g5: LineSegment StartX=-76.66 StartY=40.51 StartZ=0 EndX=-68.255 EndY=40.51 EndZ=0
    g6: LineSegment StartX=-68.255 StartY=40.51 StartZ=0 EndX=-68.255 EndY=34.5195 EndZ=0
    g7: LineSegment StartX=76.66 StartY=40.51 StartZ=0 EndX=68.255 EndY=40.51 EndZ=0
    g8: LineSegment StartX=68.255 StartY=40.51 StartZ=0 EndX=68.255 EndY=34.5195 EndZ=0
    g9: ArcOfCircle CenterX=-76.66 CenterY=45.51 CenterZ=0 NormalX=0 NormalY=0 NormalZ=1 AngleXU=0 Radius=5 StartAngle=3.14159 EndAngle=4.71239
    g10: ArcOfCircle CenterX=76.66 CenterY=45.51 CenterZ=0 NormalX=0 NormalY=0 NormalZ=1 AngleXU=0 Radius=5 StartAngle=4.71239 EndAngle=6.28319
    g11: ArcOfCircle CenterX=-106.026 CenterY=236.668 CenterZ=0 NormalX=0 NormalY=0 NormalZ=1 AngleXU=0 Radius=205.647 StartAngle=4.89711 EndAngle=5.06664
    g12: ArcOfCircle CenterX=2e-16 CenterY=-50 CenterZ=0 NormalX=0 NormalY=0 NormalZ=1 AngleXU=0 Radius=100 StartAngle=1.21654 EndAngle=1.92505
    g13: ArcOfCircle CenterX=106.026 CenterY=236.668 CenterZ=0 NormalX=0 NormalY=0 NormalZ=1 AngleXU=0 Radius=205.647 StartAngle=4.35814 EndAngle=4.52767
    g14: LineSegment StartX=0 StartY=45 StartZ=0 EndX=0 EndY=50 EndZ=0
    g15: GeomPoint X=-68.255 Y=29.5195 Z=0
    g16: LineSegment StartX=-68.255 StartY=34.5195 StartZ=0 EndX=-68.255 EndY=29.5195 EndZ=0
  constraints (41):
    c: Vertical(g0)
    c: Tangent(g0,g2) = 1.5708
    c: Tangent(g1,g3) = 1.5708
    c: Equal(g-3,g2)
    c: Symmetric(g1,g0,g-2)
    c: Tangent(g4,g3) = -1.5708
    c: Tangent(g4,g2) = -1.5708
    c: Equal(g4,g-4)
    c: Symmetric(g2,g3,g-2)
    c: Coincident(g6,g5)
    c: Vertical(g6)
    c: Horizontal(g7)
    c: Coincident(g8,g7)
    c: Symmetric(g7,g5,g-2)
    c: Tangent(g1,g9) = 1.5708
    c: Tangent(g5,g9) = -1.5708
    c: Tangent(g0,g10) = 1.5708
    c: Tangent(g7,g10) = 1.5708
    c: Equal(g9,g10)
    c: Coincident(g1,g-5)
    c: Coincident(g5,g-6)
    c: Coincident(g-7,g5)
    c: Coincident(g13,g12)
    c: Equal(g11,g-9)
    c: Equal(g12,g-8)
    c: Equal(g13,g-10)
    c: Coincident(g6,g11)
    c: Coincident(g8,g13)
    c: Symmetric(g6,g8,g-2)
    c: PointOnObject(g14,g-8)
    c: PointOnObject(g14,g12)
    c: Vertical(g14)
    c: PointOnObject(g14,g-2)
    c: DistanceY(g14,g14) = 5
    c: PointOnObject(g15,g-9)
    c: PointOnObject(g15,g-7)
    c: Coincident(g16,g6)
    c: Coincident(g16,g15)
    c: DistanceY(g16,g16) = 5
    c: Symmetric(g11,g12,g-2)
    c: Tangent(g12,g11) = 1.5708
FEATURE [Sketcher::SketchObject] Sketch016  label="sk_ref_leds_cage_cutout"
  AttachmentOffset = pos=(0,83,4) rot=(0,0,1;0rad)
  FullyConstrained = false
  MapMode = 5
  Placement = pos=(0,-4,83) rot=(1,0,0;1.5708rad)
  Support = -> [XZ_Plane002]
  expr: Constraints[109] = <<Spreadsheet>>.ref_leds_gap
  expr: Constraints[8] = <<Spreadsheet>>.ref_leds_width
  sketch-geometry (59):
    g0: LineSegment StartX=-1.4 StartY=2.31571 StartZ=0 EndX=-7.4 EndY=2.31571 EndZ=0
    g1: LineSegment StartX=-7.4 StartY=2.31571 StartZ=0 EndX=-7.4 EndY=-3.68429 EndZ=0
    g2: LineSegment StartX=-7.4 StartY=-3.68429 StartZ=0 EndX=-1.4 EndY=-3.68429 EndZ=0
    g3: LineSegment StartX=-1.4 StartY=-3.68429 StartZ=0 EndX=-1.4 EndY=2.31571 EndZ=0
    g4: LineSegment StartX=-8.4 StartY=2.31571 StartZ=0 EndX=-14.4 EndY=2.31571 EndZ=0
    g5: LineSegment StartX=-14.4 StartY=2.31571 StartZ=0 EndX=-14.4 EndY=-3.68429 EndZ=0
    g6: LineSegment StartX=-14.4 StartY=-3.68429 StartZ=0 EndX=-8.4 EndY=-3.68429 EndZ=0
    g7: LineSegment StartX=-8.4 StartY=-3.68429 StartZ=0 EndX=-8.4 EndY=2.31571 EndZ=0
    g8: LineSegment StartX=-21.4 StartY=2.31571 StartZ=0 EndX=-15.4 EndY=2.31571 EndZ=0
    g9: LineSegment StartX=-15.4 StartY=2.31571 StartZ=0 EndX=-15.4 EndY=-3.68429 EndZ=0
    g10: LineSegment StartX=-15.4 StartY=-3.68429 StartZ=0 EndX=-21.4 EndY=-3.68429 EndZ=0
    g11: LineSegment StartX=-21.4 StartY=-3.68429 StartZ=0 EndX=-21.4 EndY=2.31571 EndZ=0
    g12: LineSegment StartX=-28.4 StartY=2.31571 StartZ=0 EndX=-22.4 EndY=2.31571 EndZ=0
    g13: LineSegment StartX=-22.4 StartY=2.31571 StartZ=0 EndX=-22.4 EndY=-3.68429 EndZ=0
    g14: LineSegment StartX=-22.4 StartY=-3.68429 StartZ=0 EndX=-28.4 EndY=-3.68429 EndZ=0
    g15: LineSegment StartX=-28.4 StartY=-3.68429 StartZ=0 EndX=-28.4 EndY=2.31571 EndZ=0
    g16: LineSegment StartX=-35.4 StartY=2.31571 StartZ=0 EndX=-29.4 EndY=2.31571 EndZ=0
    g17: LineSegment StartX=-29.4 StartY=2.31571 StartZ=0 EndX=-29.4 EndY=-3.68429 EndZ=0
    g18: LineSegment StartX=-29.4 StartY=-3.68429 StartZ=0 EndX=-35.4 EndY=-3.68429 EndZ=0
    g19: LineSegment StartX=-35.4 StartY=-3.68429 StartZ=0 EndX=-35.4 EndY=2.31571 EndZ=0
    g20: LineSegment StartX=-42.4 StartY=2.31571 StartZ=0 EndX=-36.4 EndY=2.31571 EndZ=0
    g21: LineSegment StartX=-36.4 StartY=2.31571 StartZ=0 EndX=-36.4 EndY=-3.68429 EndZ=0
    g22: LineSegment StartX=-36.4 StartY=-3.68429 StartZ=0 EndX=-42.4 EndY=-3.68429 EndZ=0
    g23: LineSegment StartX=-42.4 StartY=-3.68429 StartZ=0 EndX=-42.4 EndY=2.31571 EndZ=0
    g24: LineSegment StartX=-49.4 StartY=2.31571 StartZ=0 EndX=-43.4 EndY=2.31571 EndZ=0
    g25: LineSegment StartX=-43.4 StartY=2.31571 StartZ=0 EndX=-43.4 EndY=-3.68429 EndZ=0
    g26: LineSegment StartX=-43.4 StartY=-3.68429 StartZ=0 EndX=-49.4 EndY=-3.68429 EndZ=0
    g27: LineSegment StartX=-49.4 StartY=-3.68429 StartZ=0 EndX=-49.4 EndY=2.31571 EndZ=0
    g28: LineSegment StartX=-56.4 StartY=2.31571 StartZ=0 EndX=-50.4 EndY=2.31571 EndZ=0
    g29: LineSegment StartX=-50.4 StartY=2.31571 StartZ=0 EndX=-50.4 EndY=-3.68429 EndZ=0
    g30: LineSegment StartX=-50.4 StartY=-3.68429 StartZ=0 EndX=-56.4 EndY=-3.68429 EndZ=0
    g31: LineSegment StartX=-56.4 StartY=-3.68429 StartZ=0 EndX=-56.4 EndY=2.31571 EndZ=0
    g32: LineSegment StartX=0 StartY=2.31571 StartZ=0 EndX=-1.4 EndY=2.31571 EndZ=0
    g33: LineSegment StartX=-7.4 StartY=2.31571 StartZ=0 EndX=-8.4 EndY=2.31571 EndZ=0
    g34: LineSegment StartX=-14.4 StartY=2.31571 StartZ=0 EndX=-15.4 EndY=2.31571 EndZ=0
    g35: LineSegment StartX=-21.4 StartY=2.31571 StartZ=0 EndX=-22.4 EndY=2.31571 EndZ=0
    g36: LineSegment StartX=-28.4 StartY=2.31571 StartZ=0 EndX=-29.4 EndY=2.31571 EndZ=0
    g37: LineSegment StartX=-35.4 StartY=2.31571 StartZ=0 EndX=-36.4 EndY=2.31571 EndZ=0
    g38: LineSegment StartX=-42.4 StartY=2.31571 StartZ=0 EndX=-43.4 EndY=2.31571 EndZ=0
    g39: LineSegment StartX=-49.4 StartY=2.31571 StartZ=0 EndX=-50.4 EndY=2.31571 EndZ=0
    g40: LineSegment StartX=-78.4842 StartY=-13.623 StartZ=0 EndX=-72.4842 EndY=-13.623 EndZ=0
    g41: LineSegment StartX=-72.4842 StartY=-13.623 StartZ=0 EndX=-72.4842 EndY=-7.62299 EndZ=0
    g42: LineSegment StartX=-72.4842 StartY=-7.62299 StartZ=0 EndX=-78.4842 EndY=-7.62299 EndZ=0
    g43: LineSegment StartX=-78.4842 StartY=-7.62299 StartZ=0 EndX=-78.4842 EndY=-13.623 EndZ=0
    g44: LineSegment StartX=-78.4842 StartY=-15.623 StartZ=0 EndX=-72.4842 EndY=-15.623 EndZ=0
    g45: LineSegment StartX=-72.4842 StartY=-15.623 StartZ=0 EndX=-72.4842 EndY=-21.623 EndZ=0
    g46: LineSegment StartX=-72.4842 StartY=-21.623 StartZ=0 EndX=-78.4842 EndY=-21.623 EndZ=0
    g47: LineSegment StartX=-78.4842 StartY=-21.623 StartZ=0 EndX=-78.4842 EndY=-15.623 EndZ=0
    g48: LineSegment StartX=-78.4842 StartY=-23.623 StartZ=0 EndX=-72.4842 EndY=-23.623 EndZ=0
    g49: LineSegment StartX=-72.4842 StartY=-23.623 StartZ=0 EndX=-72.4842 EndY=-29.623 EndZ=0
    g50: LineSegment StartX=-72.4842 StartY=-29.623 StartZ=0 EndX=-78.4842 EndY=-29.623 EndZ=0
    g51: LineSegment StartX=-78.4842 StartY=-29.623 StartZ=0 EndX=-78.4842 EndY=-23.623 EndZ=0
    g52: LineSegment StartX=-78.4842 StartY=-31.623 StartZ=0 EndX=-72.4842 EndY=-31.623 EndZ=0
    g53: LineSegment StartX=-72.4842 StartY=-31.623 StartZ=0 EndX=-72.4842 EndY=-37.623 EndZ=0
    g54: LineSegment StartX=-72.4842 StartY=-37.623 StartZ=0 EndX=-78.4842 EndY=-37.623 EndZ=0
    g55: LineSegment StartX=-78.4842 StartY=-37.623 StartZ=0 EndX=-78.4842 EndY=-31.623 EndZ=0
    g56: LineSegment StartX=-78.4842 StartY=-13.623 StartZ=0 EndX=-78.4842 EndY=-15.623 EndZ=0
    g57: LineSegment StartX=-78.4842 StartY=-21.623 StartZ=0 EndX=-78.4842 EndY=-23.623 EndZ=0
    g58: LineSegment StartX=-78.4842 StartY=-29.623 StartZ=0 EndX=-78.4842 EndY=-31.623 EndZ=0
  constraints (165):
    c: Coincident(g0,g1)
    c: Coincident(g1,g2)
    c: Coincident(g2,g3)
    c: Coincident(g3,g0)
    c: Horizontal(g0)
    c: Horizontal(g2)
    c: Vertical(g1)
    c: Equal(g0,g1)
    c: DistanceX(g0,g0) = 6
    c: Coincident(g4,g5)
    c: Coincident(g5,g6)
    c: Coincident(g6,g7)
    c: Coincident(g7,g4)
    c: Horizontal(g4)
    c: Horizontal(g6)
    c: Vertical(g5)
    c: Equal(g5,g4)
    c: Equal(g4,g0)
    c: Coincident(g8,g9)
    c: Coincident(g9,g10)
    c: Coincident(g10,g11)
    c: Coincident(g11,g8)
    c: Horizontal(g8)
    c: Horizontal(g10)
    c: Vertical(g9)
    c: Vertical(g11)
    c: Coincident(g12,g13)
    c: Coincident(g13,g14)
    c: Coincident(g14,g15)
    c: Coincident(g15,g12)
    c: Horizontal(g12)
    c: Horizontal(g14)
    c: Vertical(g13)
    c: Vertical(g15)
    c: Coincident(g16,g17)
    c: Coincident(g17,g18)
    c: Coincident(g18,g19)
    c: Coincident(g19,g16)
    c: Horizontal(g16)
    c: Horizontal(g18)
    c: Vertical(g17)
    c: Vertical(g19)
    c: Coincident(g20,g21)
    c: Coincident(g21,g22)
    c: Coincident(g22,g23)
    c: Coincident(g23,g20)
    c: Horizontal(g20)
    c: Horizontal(g22)
    c: Vertical(g21)
    c: Vertical(g23)
    c: Coincident(g24,g25)
    c: Coincident(g25,g26)
    c: Coincident(g26,g27)
    c: Coincident(g27,g24)
    c: Horizontal(g24)
    c: Horizontal(g26)
    c: Vertical(g25)
    c: Vertical(g27)
    c: Coincident(g28,g29)
    c: Coincident(g29,g30)
    c: Coincident(g30,g31)
    c: Coincident(g31,g28)
    c: Horizontal(g28)
    c: Horizontal(g30)
    c: Vertical(g29)
    c: Vertical(g31)
    c: Equal(g8,g11)
    c: Equal(g11,g12)
    c: Equal(g12,g15)
    c: Equal(g15,g16)
    c: Equal(g16,g19)
    c: Equal(g19,g20)
    c: Equal(g20,g23)
    c: Equal(g23,g24)
    c: Equal(g24,g27)
    c: Equal(g27,g28)
    c: Equal(g28,g31)
    c: Vertical(g7)
    c: PointOnObject(g32,g-2)
    c: Coincident(g32,g0)
    c: Horizontal(g32)
    c: Coincident(g33,g0)
    c: Coincident(g33,g4)
    c: Horizontal(g33)
    c: Coincident(g34,g4)
    c: Coincident(g34,g8)
    c: Coincident(g35,g8)
    c: Coincident(g35,g12)
    c: Coincident(g36,g12)
    c: Coincident(g36,g16)
    c: Coincident(g37,g16)
    c: Coincident(g37,g20)
    c: Coincident(g38,g20)
    c: Coincident(g38,g24)
    c: Coincident(g39,g24)
    c: Coincident(g39,g28)
    c: Horizontal(g39)
    c: Horizontal(g38)
    c: Horizontal(g37)
    c: Horizontal(g36)
    c: Horizontal(g35)
    c: Horizontal(g34)
    c: Equal(g33,g34)
    c: Equal(g34,g35)
    c: Equal(g35,g36)
    c: Equal(g36,g37)
    c: Equal(g37,g38)
    c: Equal(g38,g39)
    c: Equal(g31,g0)
    c: DistanceX(g32,g32) = 1.4
    c: Coincident(g40,g41)
    c: Coincident(g41,g42)
    c: Coincident(g42,g43)
    c: Coincident(g43,g40)
    c: Horizontal(g40)
    c: Horizontal(g42)
    c: Vertical(g41)
    c: Vertical(g43)
    c: Coincident(g44,g45)
    c: Coincident(g45,g46)
    c: Coincident(g46,g47)
    c: Coincident(g47,g44)
    c: Horizontal(g44)
    c: Horizontal(g46)
    c: Vertical(g45)
    c: Vertical(g47)
    c: Coincident(g48,g49)
    c: Coincident(g49,g50)
    c: Coincident(g50,g51)
    c: Coincident(g51,g48)
    c: Horizontal(g48)
    c: Horizontal(g50)
    c: Vertical(g49)
    c: Vertical(g51)
    c: Coincident(g52,g53)
    c: Coincident(g53,g54)
    c: Coincident(g54,g55)
    c: Coincident(g55,g52)
    c: Horizontal(g52)
    c: Horizontal(g54)
    c: Vertical(g53)
    c: Vertical(g55)
    c: Coincident(g56,g40)
    c: Coincident(g56,g44)
    c: Vertical(g56)
    c: Coincident(g57,g46)
    c: Coincident(g57,g48)
    c: Coincident(g58,g50)
    c: Coincident(g58,g52)
    c: Vertical(g58)
    c: Equal(g58,g57)
    c: Vertical(g57)
    c: DistanceX(g28,g0) = 55
    c: DistanceX(g8,g4) = 1
    c: Vertical(g3)
    c: Equal(g57,g56)
    c: DistanceY(g53,g41) = 30
    c: Equal(g41,g45)
    c: Equal(g45,g49)
    c: Equal(g49,g53)
    c: Equal(g53,g42)
    c: Equal(g42,g44)
    c: Equal(g44,g48)
    c: Equal(g48,g52)
    c: DistanceX(g42,g42) = 6
FEATURE [PartDesign::Pocket] Pocket004  label="ref_leds_cage"
  BaseFeature = -> Pocket001
  Direction = (0,1,2e-16)
  Length = 5
  Length2 = 5
  Placement = pos=(0,0,0) rot=(1,0,0;1.5708rad)
  Profile = -> Sketch016
  ReferenceAxis = -> Sketch016 [N_Axis]
  Refine = true
  Reversed = true
  Type = 1
FEATURE [PartDesign::Mirrored] Mirrored  label="mirror_ref_leds_cage"
  BaseFeature = -> Pocket004
  MirrorPlane = -> Sketch016 [V_Axis]
  Originals = -> [Pocket004]
  Placement = pos=(0,0,0) rot=(1,0,0;1.5708rad)
  Refine = true
FEATURE [Sketcher::SketchObject] Sketch018  label="sk_ref_leds_back_cutout"
  AttachmentOffset = pos=(0,0,10) rot=(0,0,1;0rad)
  ExternalGeometry = -> [Sketch016]
  FullyConstrained = false
  MapMode = 5
  Placement = pos=(0,-10,-2.2e-15) rot=(1,0,0;1.5708rad)
  Support = -> [XZ_Plane002]
  sketch-geometry (14):
    g0: LineSegment StartX=-57.3865 StartY=90.3157 StartZ=0 EndX=0 EndY=90.3157 EndZ=0
    g1: LineSegment StartX=0 StartY=90.3157 StartZ=0 EndX=0 EndY=78.3157 EndZ=0
    g2: LineSegment StartX=0 StartY=78.3157 StartZ=0 EndX=-70.1036 EndY=78.3157 EndZ=0
    g3: LineSegment StartX=-56.4 StartY=85.3157 StartZ=0 EndX=-56.4 EndY=90.3157 EndZ=0
    g4: LineSegment StartX=-70.1036 StartY=42.8533 StartZ=0 EndX=-82.1036 EndY=42.8533 EndZ=0
    g5: LineSegment StartX=-82.1036 StartY=42.8533 StartZ=0 EndX=-82.1036 EndY=76.7035 EndZ=0
    g6: LineSegment StartX=-70.1036 StartY=78.3157 StartZ=0 EndX=-70.1036 EndY=42.8533 EndZ=0
    g7: LineSegment StartX=-72.4842 StartY=75.377 StartZ=0 EndX=-70.1036 EndY=75.377 EndZ=0
    g8: LineSegment StartX=-78.4842 StartY=75.377 StartZ=0 EndX=-82.1036 EndY=75.377 EndZ=0
    g9: LineSegment StartX=-82.1036 StartY=76.7035 StartZ=0 EndX=-78.767 EndY=76.7035 EndZ=0
    g10: LineSegment StartX=-75.8155 StartY=78.6087 StartZ=0 EndX=-74.4233 EndY=81.6896 EndZ=0
    g11: LineSegment StartX=-67.7085 StartY=87.4467 StartZ=0 EndX=-57.3865 EndY=90.3157 EndZ=0
    g12: ArcOfCircle CenterX=-64.9139 CenterY=77.3927 CenterZ=0 NormalX=0 NormalY=0 NormalZ=1 AngleXU=0 Radius=10.4351 StartAngle=1.84191 EndAngle=2.71719
    g13: ArcOfCircle CenterX=-78.767 CenterY=79.9424 CenterZ=0 NormalX=0 NormalY=0 NormalZ=1 AngleXU=0 Radius=3.23893 StartAngle=4.71239 EndAngle=5.85878
  constraints (31):
    c: Coincident(g0,g1)
    c: Coincident(g1,g2)
    c: Horizontal(g2)
    c: Vertical(g1)
    c: PointOnObject(g3,g0)
    c: Vertical(g3)
    c: Horizontal(g0)
    c: Coincident(g4,g5)
    c: Coincident(g6,g4)
    c: Horizontal(g4)
    c: Vertical(g5)
    c: Vertical(g6)
    c: Coincident(g7,g-3)
    c: PointOnObject(g7,g6)
    c: Horizontal(g7)
    c: Coincident(g8,g-3)
    c: PointOnObject(g8,g5)
    c: Horizontal(g8)
    c: DistanceY(g1,g1) = 12
    c: Equal(g4,g1)
    c: Coincident(g2,g6)
    c: DistanceY(g3,g3) = 5
    c: PointOnObject(g0,g-2)
    c: Coincident(g3,g-4)
    c: Coincident(g9,g5)
    c: Horizontal(g9)
    c: Coincident(g11,g0)
    c: Tangent(g10,g12) = 1.5708
    c: Tangent(g11,g12) = 1.5708
    c: Tangent(g9,g13) = -1.5708
    c: Tangent(g10,g13) = -1.5708
FEATURE [Sketcher::SketchObject] Sketch017  label="sk_ref_leds_diffusor_cutout"
  AttachmentOffset = pos=(0,0,4) rot=(0,0,1;0rad)
  ExternalGeometry = -> [Sketch016,Sketch018]
  FullyConstrained = false
  MapMode = 5
  Placement = pos=(0,-4,-9e-16) rot=(1,0,0;1.5708rad)
  Support = -> [XZ_Plane002]
  expr: Constraints[14] = <<Spreadsheet>>.ref_leds_width + 1
  expr: Constraints[18] = <<Spreadsheet>>.ref_leds_gap / 2
  sketch-geometry (13):
    g0: LineSegment StartX=-57.1 StartY=85.8157 StartZ=0 EndX=0 EndY=85.8157 EndZ=0
    g1: LineSegment StartX=0 StartY=85.8157 StartZ=0 EndX=0 EndY=78.8157 EndZ=0
    g2: LineSegment StartX=0 StartY=78.8157 StartZ=0 EndX=-57.1 EndY=78.8157 EndZ=0
    g3: LineSegment StartX=-57.1 StartY=78.8157 StartZ=0 EndX=-57.1 EndY=85.8157 EndZ=0
    g4: LineSegment StartX=-56.4 StartY=85.3157 StartZ=0 EndX=-56.4 EndY=85.8157 EndZ=0
    g5: LineSegment StartX=-56.4 StartY=79.3157 StartZ=0 EndX=-56.4 EndY=78.8157 EndZ=0
    g6: LineSegment StartX=-56.4 StartY=79.3157 StartZ=0 EndX=-57.1 EndY=79.3157 EndZ=0
    g7: LineSegment StartX=-72.0921 StartY=75.9671 StartZ=0 EndX=-72.0921 EndY=42.8533 EndZ=0
    g8: LineSegment StartX=-72.0921 StartY=42.8533 StartZ=0 EndX=-79.2328 EndY=42.8533 EndZ=0
    g9: LineSegment StartX=-79.2328 StartY=42.8533 StartZ=0 EndX=-79.2328 EndY=75.9671 EndZ=0
    g10: LineSegment StartX=-72.4842 StartY=75.377 StartZ=0 EndX=-72.0921 EndY=75.377 EndZ=0
    g11: LineSegment StartX=-72.4842 StartY=45.377 StartZ=0 EndX=-72.4842 EndY=42.8533 EndZ=0
    g12: LineSegment StartX=-79.2328 StartY=75.9671 StartZ=0 EndX=-72.0921 EndY=75.9671 EndZ=0
  constraints (35):
    c: Coincident(g0,g1)
    c: Coincident(g1,g2)
    c: Coincident(g2,g3)
    c: Coincident(g3,g0)
    c: Horizontal(g2)
    c: Vertical(g1)
    c: Vertical(g3)
    c: Coincident(g4,g-3)
    c: PointOnObject(g4,g0)
    c: Vertical(g4)
    c: Coincident(g5,g-3)
    c: PointOnObject(g5,g2)
    c: Vertical(g5)
    c: Equal(g4,g5)
    c: DistanceY(g3,g3) = 7
    c: Coincident(g6,g5)
    c: PointOnObject(g6,g3)
    c: Horizontal(g6)
    c: DistanceX(g6,g6) = 0.7
    c: Coincident(g7,g8)
    c: Coincident(g8,g9)
    c: Horizontal(g8)
    c: Vertical(g7)
    c: Vertical(g9)
    c: PointOnObject(g10,g7)
    c: Horizontal(g10)
    c: Coincident(g11,g-4)
    c: PointOnObject(g11,g8)
    c: Vertical(g11)
    c: PointOnObject(g1,g-2)
    c: Horizontal(g0)
    c: Coincident(g12,g9)
    c: Coincident(g12,g7)
    c: Horizontal(g12)
    c: PointOnObject(g11,g-5)
FEATURE [PartDesign::Pocket] Pocket005  label="ref_leds_diffusor_cutout"
  BaseFeature = -> Mirrored
  Direction = (0,1,2e-16)
  Length = 1.4
  Length2 = 5
  Placement = pos=(0,0,0) rot=(1,0,0;1.5708rad)
  Profile = -> Sketch017
  ReferenceAxis = -> Sketch017 [N_Axis]
  Refine = true
  Reversed = true
  Type = 0
  expr: Length = <<Spreadsheet>>.ref_leds_gap
FEATURE [PartDesign::Mirrored] Mirrored001  label="mirror_ref_leds_diffusor_cutout"
  BaseFeature = -> Pocket005
  MirrorPlane = -> Sketch017 [V_Axis]
  Originals = -> [Pocket005]
  Placement = pos=(0,0,0) rot=(1,0,0;1.5708rad)
  Refine = true
FEATURE [PartDesign::Pocket] Pocket006  label="ref_leds_back_cutout"
  BaseFeature = -> Mirrored001
  Direction = (0,1,2e-16)
  Length = 2.5
  Length2 = 5
  Placement = pos=(0,0,0) rot=(1,0,0;1.5708rad)
  Profile = -> Sketch018
  ReferenceAxis = -> Sketch018 [N_Axis]
  Refine = true
  Type = 0
FEATURE [PartDesign::Mirrored] Mirrored002  label="mirror_ref_leds_back_cutout"
  BaseFeature = -> Pocket006
  MirrorPlane = -> Sketch018 [V_Axis]
  Originals = -> [Pocket006]
  Placement = pos=(0,0,0) rot=(1,0,0;1.5708rad)
  Refine = true
FEATURE [Sketcher::SketchObject] Sketch021
  FullyConstrained = true
  MapMode = 5
  Placement = pos=(0,0,0) rot=(1,0,0;1.5708rad)
  Support = -> [XZ_Plane004]
  expr: Constraints[38] = <<Spreadsheet>>.ref_leds_width
  expr: Constraints[50] = <<Spreadsheet>>.ref_leds_gap
  expr: Constraints[54] = <<Spreadsheet>>.ref_leds_gap / 2
  expr: Constraints[65] = <<Spreadsheet>>.ref_leds_gap / 2
  expr: Constraints[66] = <<Spreadsheet>>.ref_leds_width + 1
  sketch-geometry (24):
    g0: LineSegment StartX=-3 StartY=0.7 StartZ=0 EndX=3 EndY=0.7 EndZ=0
    g1: LineSegment StartX=3 StartY=0.7 StartZ=0 EndX=3 EndY=6.7 EndZ=0
    g2: LineSegment StartX=3 StartY=6.7 StartZ=0 EndX=-3 EndY=6.7 EndZ=0
    g3: LineSegment StartX=-3 StartY=6.7 StartZ=0 EndX=-3 EndY=0.7 EndZ=0
    g4: LineSegment StartX=-3 StartY=8.1 StartZ=0 EndX=3 EndY=8.1 EndZ=0
    g5: LineSegment StartX=3 StartY=8.1 StartZ=0 EndX=3 EndY=14.1 EndZ=0
    g6: LineSegment StartX=3 StartY=14.1 StartZ=0 EndX=-3 EndY=14.1 EndZ=0
    g7: LineSegment StartX=-3 StartY=14.1 StartZ=0 EndX=-3 EndY=8.1 EndZ=0
    g8: LineSegment StartX=-3 StartY=15.5 StartZ=0 EndX=3 EndY=15.5 EndZ=0
    g9: LineSegment StartX=3 StartY=15.5 StartZ=0 EndX=3 EndY=21.5 EndZ=0
    g10: LineSegment StartX=3 StartY=21.5 StartZ=0 EndX=-3 EndY=21.5 EndZ=0
    g11: LineSegment StartX=-3 StartY=21.5 StartZ=0 EndX=-3 EndY=15.5 EndZ=0
    g12: LineSegment StartX=-3 StartY=22.9 StartZ=0 EndX=3 EndY=22.9 EndZ=0
    g13: LineSegment StartX=3 StartY=22.9 StartZ=0 EndX=3 EndY=28.9 EndZ=0
    g14: LineSegment StartX=3 StartY=28.9 StartZ=0 EndX=-3 EndY=28.9 EndZ=0
    g15: LineSegment StartX=-3 StartY=28.9 StartZ=0 EndX=-3 EndY=22.9 EndZ=0
    g16: LineSegment StartX=3 StartY=6.7 StartZ=0 EndX=3 EndY=8.1 EndZ=0
    g17: LineSegment StartX=3 StartY=14.1 StartZ=0 EndX=3 EndY=15.5 EndZ=0
    g18: LineSegment StartX=3 StartY=21.5 StartZ=0 EndX=3 EndY=22.9 EndZ=0
    g19: LineSegment StartX=3 StartY=0.7 StartZ=0 EndX=3 EndY=0 EndZ=0
    g20: LineSegment StartX=-3.5 StartY=0 StartZ=0 EndX=3.5 EndY=0 EndZ=0
    g21: LineSegment StartX=3.5 StartY=0 StartZ=0 EndX=3.5 EndY=29.6 EndZ=0
    g22: LineSegment StartX=3.5 StartY=29.6 StartZ=0 EndX=-3.5 EndY=29.6 EndZ=0
    g23: LineSegment StartX=-3.5 StartY=29.6 StartZ=0 EndX=-3.5 EndY=0 EndZ=0
  constraints (67):
    c: Coincident(g0,g1)
    c: Coincident(g1,g2)
    c: Coincident(g2,g3)
    c: Coincident(g3,g0)
    c: Horizontal(g0)
    c: Vertical(g1)
    c: Vertical(g3)
    c: Coincident(g4,g5)
    c: Coincident(g5,g6)
    c: Coincident(g6,g7)
    c: Coincident(g7,g4)
    c: Horizontal(g4)
    c: Horizontal(g6)
    c: Vertical(g5)
    c: Vertical(g7)
    c: Coincident(g8,g9)
    c: Coincident(g9,g10)
    c: Coincident(g10,g11)
    c: Coincident(g11,g8)
    c: Horizontal(g8)
    c: Horizontal(g10)
    c: Vertical(g9)
    c: Vertical(g11)
    c: Coincident(g12,g13)
    c: Coincident(g13,g14)
    c: Coincident(g14,g15)
    c: Coincident(g15,g12)
    c: Horizontal(g12)
    c: Horizontal(g14)
    c: Vertical(g13)
    c: Vertical(g15)
    c: Equal(g3,g2)
    c: Equal(g2,g7)
    c: Equal(g7,g6)
    c: Equal(g6,g11)
    c: Equal(g11,g10)
    c: Equal(g10,g15)
    c: Equal(g15,g14)
    c: DistanceY(g1,g1) = 6
    c: Coincident(g16,g1)
    c: Coincident(g16,g4)
    c: Vertical(g16)
    c: Coincident(g17,g5)
    c: Coincident(g17,g8)
    c: Vertical(g17)
    c: Coincident(g18,g9)
    c: Coincident(g18,g12)
    c: Vertical(g18)
    c: Equal(g16,g17)
    c: Equal(g17,g18)
    c: DistanceY(g16,g16) = 1.4
    c: Coincident(g19,g0)
    c: PointOnObject(g19,g-1)
    c: Vertical(g19)
    c: DistanceY(g19,g19) = 0.7
    c: Symmetric(g2,g1,g-2)
    c: Coincident(g20,g21)
    c: Coincident(g21,g22)
    c: Coincident(g22,g23)
    c: Coincident(g23,g20)
    c: Horizontal(g20)
    c: Vertical(g21)
    c: Vertical(g23)
    c: PointOnObject(g20,g-1)
    c: Symmetric(g22,g21,g-2)
    c: DistanceY(g13,g21) = 0.7
    c: DistanceX(g22,g22) = 7
FEATURE [Sketcher::SketchObject] Sketch022
  ExternalGeometry = -> [Sketch021]
  FullyConstrained = true
  MapMode = 5
  Placement = pos=(0,0,0) rot=(1,0,0;1.5708rad)
  Support = -> [XZ_Plane004]
  expr: Constraints[9] = <<Spreadsheet>>.ref_leds_width + 1
  sketch-geometry (4):
    g0: LineSegment StartX=-3.5 StartY=0 StartZ=0 EndX=3.5 EndY=0 EndZ=0
    g1: LineSegment StartX=3.5 StartY=0 StartZ=0 EndX=3.5 EndY=29.6 EndZ=0
    g2: LineSegment StartX=3.5 StartY=29.6 StartZ=0 EndX=-3.5 EndY=29.6 EndZ=0
    g3: LineSegment StartX=-3.5 StartY=29.6 StartZ=0 EndX=-3.5 EndY=0 EndZ=0
  constraints (11):
    c: Coincident(g0,g1)
    c: Coincident(g1,g2)
    c: Coincident(g2,g3)
    c: Coincident(g3,g0)
    c: Horizontal(g0)
    c: Horizontal(g2)
    c: Vertical(g1)
    c: Vertical(g3)
    c: PointOnObject(g0,g-1)
    c: DistanceX(g2,g2) = 7
    c: Coincident(g2,g-3)
FEATURE [PartDesign::Pad] Pad010
  Direction = (0,-1,-2e-16)
  Length = 1
  Length2 = 10
  Placement = pos=(0,0,0) rot=(1,0,0;1.5708rad)
  Profile = -> Sketch022
  ReferenceAxis = -> Sketch022 [N_Axis]
  Refine = true
  Type = 0
FEATURE [PartDesign::Pad] Pad011
  BaseFeature = -> Pad010
  Direction = (0,-1,-2e-16)
  Length = 1.19
  Length2 = 10
  Placement = pos=(0,0,0) rot=(1,0,0;1.5708rad)
  Profile = -> Sketch021
  ReferenceAxis = -> Sketch021 [N_Axis]
  Refine = true
  Reversed = true
  Type = 0
FEATURE [PartDesign::Body] Body004  label="led_diffusor_side"
  Group = -> [Sketch021,Sketch022,Pad010,Pad011]
  Origin = -> Origin004
  Placement = pos=(-74,-102,45.5) rot=(0,0,1;0rad)
  Tip = -> Pad011
FEATURE [Part::FeaturePython] Clone  label="led_diffusor_side001"  # Draft clone (typed FeaturePython)
  AttacherType = Attacher::AttachEngine3D
  Fuse = false
  Objects = -> [Body004]
  Placement = pos=(74,-102,45.5) rot=(0,0,1;0rad)
  Scale = (1,1,1)
FEATURE [PartDesign::Pad] Pad012  label="backside"
  BaseFeature = -> Pad
  Direction = (0,-1,-2e-16)
  Length = 25
  Length2 = 10
  Placement = pos=(0,0,0) rot=(1,0,0;1.5708rad)
  Profile = -> Sketch012
  ReferenceAxis = -> Sketch012 [N_Axis]
  Refine = true
  Reversed = true
  Type = 0
FEATURE [PartDesign::Pocket] Pocket007  label="mount_cutout"
  BaseFeature = -> Pad012
  Direction = (0,1,2e-16)
  Length = 5
  Length2 = 5
  Placement = pos=(0,0,0) rot=(1,0,0;1.5708rad)
  Profile = -> Sketch013
  ReferenceAxis = -> Sketch013 [N_Axis]
  Refine = true
  Reversed = true
  Type = 1
FEATURE [PartDesign::Pocket] Pocket008  label="frame_cutout"
  BaseFeature = -> Pocket007
  Direction = (0,1,2e-16)
  Length = 30
  Length2 = 5
  Placement = pos=(0,0,0) rot=(1,0,0;1.5708rad)
  Profile = -> Sketch015
  ReferenceAxis = -> Sketch015 [N_Axis]
  Refine = true
  Type = 0
FEATURE [Sketcher::SketchObject] Sketch023  label="sk_mount_inlay"
  AttachmentOffset = pos=(0,0,7) rot=(0,0,1;0rad)
  ExternalGeometry = -> [Sketch013]
  FullyConstrained = true
  MapMode = 5
  Placement = pos=(0,-7,-1.6e-15) rot=(1,0,0;1.5708rad)
  Support = -> [XZ_Plane]
  sketch-geometry (2):
    g0: Circle CenterX=-28 CenterY=14 CenterZ=0 NormalX=0 NormalY=0 NormalZ=1 AngleXU=0 Radius=5
    g1: Circle CenterX=28 CenterY=14 CenterZ=0 NormalX=0 NormalY=0 NormalZ=1 AngleXU=0 Radius=5
  constraints (4):
    c: Coincident(g0,g-3)
    c: Coincident(g1,g-4)
    c: Equal(g0,g1)
    c: Diameter(g0) = 10
FEATURE [PartDesign::Pocket] Pocket009  label="mount_inlay"
  BaseFeature = -> Pocket008
  Direction = (0,1,2e-16)
  Length = 4
  Length2 = 5
  Placement = pos=(0,0,0) rot=(1,0,0;1.5708rad)
  Profile = -> Sketch023
  ReferenceAxis = -> Sketch023 [N_Axis]
  Refine = true
  Type = 0
FEATURE [Sketcher::SketchObject] Sketch024  label="sk_standoffs"
  AttachmentOffset = pos=(0,0,-23) rot=(0,0,1;0rad)
  ExternalGeometry = -> [Sketch011,Sketch015]
  FullyConstrained = true
  MapMode = 5
  Placement = pos=(0,23,5.1e-15) rot=(1,0,0;1.5708rad)
  Support = -> [XZ_Plane]
  sketch-geometry (4):
    g0: Circle CenterX=-79.613 CenterY=81.6659 CenterZ=0 NormalX=0 NormalY=0 NormalZ=1 AngleXU=0 Radius=4.5
    g1: LineSegment StartX=-79.1329 StartY=89.0613 StartZ=0 EndX=-79.613 EndY=81.6659 EndZ=0
    g2: LineSegment StartX=-79.613 StartY=81.6659 StartZ=0 EndX=-86.66 EndY=79.3718 EndZ=0
    g3: Circle CenterX=79.613 CenterY=81.6659 CenterZ=0 NormalX=0 NormalY=0 NormalZ=1 AngleXU=0 Radius=4.5
  constraints (9):
    c: PointOnObject(g0,g-4)
    c: Coincident(g1,g-3)
    c: Coincident(g1,g0)
    c: Coincident(g2,g0)
    c: Coincident(g2,g-3)
    c: Equal(g1,g2)
    c: Diameter(g0) = 9
    c: Symmetric(g3,g0,g-2)
    c: Equal(g3,g0)
FEATURE [PartDesign::Pad] Pad013  label="standoffs"
  BaseFeature = -> Pocket009
  Direction = (0,-1,-2e-16)
  Length = 30
  Length2 = 10
  Placement = pos=(0,0,0) rot=(1,0,0;1.5708rad)
  Profile = -> Sketch024
  ReferenceAxis = -> Sketch024 [N_Axis]
  Refine = true
  Type = 0
FEATURE [Sketcher::SketchObject] Sketch025  label="sk_standoff"
  AttachmentOffset = pos=(0,0,9) rot=(0,0,1;0rad)
  ExternalGeometry = -> [Sketch005]
  FullyConstrained = true
  MapMode = 5
  Placement = pos=(0,-9,-2e-15) rot=(1,0,0;1.5708rad)
  Support = -> [XZ_Plane002]
  sketch-geometry (6):
    g0: Circle CenterX=79.613 CenterY=81.6659 CenterZ=0 NormalX=0 NormalY=0 NormalZ=1 AngleXU=0 Radius=4.5
    g1: Circle CenterX=-79.613 CenterY=81.6659 CenterZ=0 NormalX=0 NormalY=0 NormalZ=1 AngleXU=0 Radius=4.5
    g2: LineSegment StartX=79.613 StartY=81.6659 StartZ=0 EndX=79.1329 EndY=89.0613 EndZ=0
    g3: LineSegment StartX=79.613 StartY=81.6659 StartZ=0 EndX=86.66 EndY=79.3718 EndZ=0
    g4: Circle CenterX=-79.613 CenterY=81.6659 CenterZ=0 NormalX=0 NormalY=0 NormalZ=1 AngleXU=0 Radius=2.49
    g5: Circle CenterX=79.613 CenterY=81.6659 CenterZ=0 NormalX=0 NormalY=0 NormalZ=1 AngleXU=0 Radius=2.49
  constraints (13):
    c: Symmetric(g0,g1,g-2)
    c: PointOnObject(g0,g-3)
    c: Coincident(g2,g0)
    c: Coincident(g2,g-4)
    c: Coincident(g3,g0)
    c: Coincident(g3,g-4)
    c: Equal(g2,g3)
    c: Diameter(g0) = 9
    c: Equal(g1,g0)
    c: Coincident(g4,g1)
    c: Coincident(g5,g0)
    c: Equal(g4,g5)
    c: Diameter(g4) = 4.98
FEATURE [PartDesign::Pad] Pad014  label="standoff"
  BaseFeature = -> Mirrored002
  Direction = (0,-1,-2e-16)
  Length = 1
  Length2 = 10
  Placement = pos=(0,0,0) rot=(1,0,0;1.5708rad)
  Profile = -> Sketch025
  ReferenceAxis = -> Sketch025 [N_Axis]
  Refine = true
  Type = 0
FEATURE [Sketcher::SketchObject] Sketch026  label="sk_standoff_cutouts"
  AttachmentOffset = pos=(0,0,10) rot=(0,0,1;0rad)
  ExternalGeometry = -> [Sketch025]
  FullyConstrained = true
  MapMode = 5
  Placement = pos=(0,-10,-2.2e-15) rot=(1,0,0;1.5708rad)
  Support = -> [XZ_Plane002]
  sketch-geometry (2):
    g0: Circle CenterX=79.613 CenterY=81.6659 CenterZ=0 NormalX=0 NormalY=0 NormalZ=1 AngleXU=0 Radius=2.49
    g1: Circle CenterX=-79.613 CenterY=81.6659 CenterZ=0 NormalX=0 NormalY=0 NormalZ=1 AngleXU=0 Radius=2.49
  constraints (4):
    c: Coincident(g0,g-3)
    c: Symmetric(g1,g0,g-2)
    c: Equal(g1,g0)
    c: Equal(g-3,g0)
FEATURE [PartDesign::Pocket] Pocket010  label="standoff_cutouts"
  BaseFeature = -> Pad014
  Direction = (0,1,2e-16)
  Length = 5
  Length2 = 5
  Placement = pos=(0,0,0) rot=(1,0,0;1.5708rad)
  Profile = -> Sketch026
  ReferenceAxis = -> Sketch026 [N_Axis]
  Refine = true
  Type = 0
FEATURE [Sketcher::SketchObject] Sketch027  label="sk_front_magnet_cutouts"
  AttachmentOffset = pos=(0,0,10) rot=(0,0,1;0rad)
  ExternalGeometry = -> [Sketch005]
  FullyConstrained = true
  MapMode = 5
  Placement = pos=(0,-10,-2.2e-15) rot=(1,0,0;1.5708rad)
  Support = -> [XZ_Plane002]
  sketch-geometry (4):
    g0: Circle CenterX=-66.7905 CenterY=6.46447 CenterZ=0 NormalX=0 NormalY=0 NormalZ=1 AngleXU=0 Radius=2.75
    g1: Circle CenterX=66.7905 CenterY=6.46447 CenterZ=0 NormalX=0 NormalY=0 NormalZ=1 AngleXU=0 Radius=2.75
    g2: LineSegment StartX=-68.255 StartY=9e-16 StartZ=0 EndX=-66.7905 EndY=6.46447 EndZ=0
    g3: LineSegment StartX=-73.255 StartY=5 StartZ=0 EndX=-66.7905 EndY=6.46447 EndZ=0
  constraints (10):
    c: PointOnObject(g0,g-3)
    c: Symmetric(g0,g1,g-2)
    c: Equal(g0,g1)
    c: Diameter(g0) = 5.5
    c: Coincident(g2,g-4)
    c: Coincident(g2,g0)
    c: Coincident(g3,g-4)
    c: Coincident(g3,g0)
    c: Equal(g2,g3)
    c: Distance(g2) = 6.62827
FEATURE [Sketcher::SketchObject] Sketch028  label="sk_magnet_cutouts"
  AttachmentOffset = pos=(0,0,7) rot=(0,0,1;0rad)
  ExternalGeometry = -> [Sketch011]
  FullyConstrained = true
  MapMode = 5
  Placement = pos=(0,-7,-1.6e-15) rot=(1,0,0;1.5708rad)
  Support = -> [XZ_Plane]
  sketch-geometry (4):
    g0: Circle CenterX=-66.7891 CenterY=6.46591 CenterZ=0 NormalX=0 NormalY=0 NormalZ=1 AngleXU=0 Radius=2.75
    g1: Circle CenterX=66.7891 CenterY=6.46591 CenterZ=0 NormalX=0 NormalY=0 NormalZ=1 AngleXU=0 Radius=2.75
    g2: LineSegment StartX=-68.255 StartY=0 StartZ=0 EndX=-66.7891 EndY=6.46591 EndZ=0
    g3: LineSegment StartX=-73.255 StartY=5 StartZ=0 EndX=-66.7891 EndY=6.46591 EndZ=0
  constraints (9):
    c: Symmetric(g0,g1,g-2)
    c: Equal(g0,g1)
    c: Diameter(g0) = 5.5
    c: Coincident(g2,g-3)
    c: Coincident(g2,g0)
    c: Coincident(g3,g-3)
    c: Coincident(g3,g0)
    c: Equal(g2,g3)
    c: Distance(g2) = 6.63
FEATURE [PartDesign::Pocket] Pocket012  label="magnet_cutouts"
  BaseFeature = -> Pad013
  Direction = (0,1,2e-16)
  Length = 1.5
  Length2 = 5
  Placement = pos=(0,0,0) rot=(1,0,0;1.5708rad)
  Profile = -> Sketch028
  ReferenceAxis = -> Sketch028 [N_Axis]
  Refine = true
  Type = 0
FEATURE [Sketcher::SketchObject] Sketch029  label="sk_standoff_holes"
  AttachmentOffset = pos=(0,0,-25) rot=(0,0,1;0rad)
  ExternalGeometry = -> [Sketch024]
  FullyConstrained = true
  MapMode = 5
  Placement = pos=(0,25,5.6e-15) rot=(1,0,0;1.5708rad)
  Support = -> [XZ_Plane]
  sketch-geometry (2):
    g0: Circle CenterX=-79.613 CenterY=81.6659 CenterZ=0 NormalX=0 NormalY=0 NormalZ=1 AngleXU=0 Radius=1.55
    g1: Circle CenterX=79.613 CenterY=81.6659 CenterZ=0 NormalX=0 NormalY=0 NormalZ=1 AngleXU=0 Radius=1.55
  constraints (4):
    c: Coincident(g0,g-3)
    c: Symmetric(g0,g1,g-2)
    c: Equal(g0,g1)
    c: Diameter(g0) = 3.1
FEATURE [PartDesign::Pocket] Pocket013  label="standoff_holes"
  BaseFeature = -> Pocket012
  Direction = (0,1,2e-16)
  Length = 5
  Length2 = 5
  Placement = pos=(0,0,0) rot=(1,0,0;1.5708rad)
  Profile = -> Sketch029
  ReferenceAxis = -> Sketch029 [N_Axis]
  Refine = true
  Reversed = true
  Type = 1
FEATURE [Sketcher::SketchObject] Sketch030  label="sk_standoff_back_sunk"
  AttachmentOffset = pos=(0,0,-25) rot=(0,0,1;0rad)
  ExternalGeometry = -> [Sketch029]
  FullyConstrained = true
  MapMode = 5
  Placement = pos=(0,25,5.6e-15) rot=(1,0,0;1.5708rad)
  Support = -> [XZ_Plane]
  sketch-geometry (2):
    g0: Circle CenterX=-79.613 CenterY=81.6659 CenterZ=0 NormalX=0 NormalY=0 NormalZ=1 AngleXU=0 Radius=2.5
    g1: Circle CenterX=79.613 CenterY=81.6659 CenterZ=0 NormalX=0 NormalY=0 NormalZ=1 AngleXU=0 Radius=2.5
  constraints (4):
    c: Coincident(g0,g-3)
    c: Symmetric(g0,g1,g-2)
    c: Equal(g0,g1)
    c: Diameter(g0) = 5
FEATURE [PartDesign::Pocket] Pocket014  label="standoff_back_sunk"
  BaseFeature = -> Pocket013
  Direction = (0,1,2e-16)
  Length = 3
  Length2 = 5
  Placement = pos=(0,0,0) rot=(1,0,0;1.5708rad)
  Profile = -> Sketch030
  ReferenceAxis = -> Sketch030 [N_Axis]
  Refine = true
  Reversed = true
  Type = 0
FEATURE [Sketcher::SketchObject] Sketch002  label="sk_display"
  FullyConstrained = true
  MapMode = 5
  Placement = pos=(0,0,0) rot=(1,0,0;1.5708rad)
  Support = -> [XZ_Plane001]
  expr: Constraints[8] = <<Spreadsheet>>.display_width
  expr: Constraints[9] = <<Spreadsheet>>.display_height
  sketch-geometry (4):
    g0: LineSegment StartX=-59.65 StartY=34.35 StartZ=0 EndX=59.65 EndY=34.35 EndZ=0
    g1: LineSegment StartX=59.65 StartY=34.35 StartZ=0 EndX=59.65 EndY=-34.35 EndZ=0
    g2: LineSegment StartX=59.65 StartY=-34.35 StartZ=0 EndX=-59.65 EndY=-34.35 EndZ=0
    g3: LineSegment StartX=-59.65 StartY=-34.35 StartZ=0 EndX=-59.65 EndY=34.35 EndZ=0
  constraints (11):
    c: Coincident(g0,g1)
    c: Coincident(g1,g2)
    c: Coincident(g2,g3)
    c: Coincident(g3,g0)
    c: Horizontal(g0)
    c: Horizontal(g2)
    c: Vertical(g1)
    c: Vertical(g3)
    c: DistanceX(g0,g0) = 119.3
    c: DistanceY(g1,g1) = 68.7
    c: Symmetric(g0,g1,g-1)
FEATURE [PartDesign::Pad] Pad001  label="display"
  Direction = (0,-1,-2e-16)
  Length = 3.6
  Length2 = 10
  Placement = pos=(0,0,0) rot=(1,0,0;1.5708rad)
  Profile = -> Sketch002
  ReferenceAxis = -> Sketch002 [N_Axis]
  Refine = true
  Type = 0
FEATURE [Sketcher::SketchObject] Sketch004
  AttachmentOffset = pos=(0,0,-1) rot=(0,0,1;0rad)
  ExternalGeometry = -> [Sketch002]
  FullyConstrained = true
  MapMode = 5
  Placement = pos=(0,1,2e-16) rot=(1,0,0;1.5708rad)
  Support = -> [XZ_Plane001]
  sketch-geometry (4):
    g0: LineSegment StartX=-33.65 StartY=21.35 StartZ=0 EndX=-59.65 EndY=21.35 EndZ=0
    g1: LineSegment StartX=-59.65 StartY=21.35 StartZ=0 EndX=-59.65 EndY=-34.35 EndZ=0
    g2: LineSegment StartX=-59.65 StartY=-34.35 StartZ=0 EndX=-33.65 EndY=-34.35 EndZ=0
    g3: LineSegment StartX=-33.65 StartY=-34.35 StartZ=0 EndX=-33.65 EndY=21.35 EndZ=0
  constraints (11):
    c: Coincident(g0,g1)
    c: Coincident(g1,g2)
    c: Coincident(g2,g3)
    c: Coincident(g3,g0)
    c: Horizontal(g0)
    c: Horizontal(g2)
    c: Vertical(g1)
    c: Vertical(g3)
    c: DistanceX(g0,g0) = 26
    c: Coincident(g1,g-3)
    c: DistanceY(g0,g-3) = 13
FEATURE [Sketcher::SketchObject] Sketch003  label="sk_screen"
  AttachmentOffset = pos=(0,0,3.5) rot=(0,0,1;0rad)
  ExternalGeometry = -> [Sketch002]
  FullyConstrained = true
  MapMode = 5
  Placement = pos=(0,-3.5,-8e-16) rot=(1,0,0;1.5708rad)
  Support = -> [XZ_Plane001]
  expr: Constraints[10] = <<Spreadsheet>>.screen_offset_left
  expr: Constraints[7] = <<Spreadsheet>>.screen_width
  expr: Constraints[8] = <<Spreadsheet>>.screen_height
  sketch-geometry (4):
    g0: LineSegment StartX=-51.65 StartY=30.8 StartZ=0 EndX=57.95 EndY=30.8 EndZ=0
    g1: LineSegment StartX=57.95 StartY=30.8 StartZ=0 EndX=57.95 EndY=-30.8 EndZ=0
    g2: LineSegment StartX=57.95 StartY=-30.8 StartZ=0 EndX=-51.65 EndY=-30.8 EndZ=0
    g3: LineSegment StartX=-51.65 StartY=-30.8 StartZ=0 EndX=-51.65 EndY=30.8 EndZ=0
  constraints (11):
    c: Coincident(g0,g1)
    c: Coincident(g1,g2)
    c: Coincident(g2,g3)
    c: Coincident(g3,g0)
    c: Horizontal(g0)
    c: Horizontal(g2)
    c: Vertical(g1)
    c: DistanceX(g0,g0) = 109.6
    c: DistanceY(g1,g1) = 61.6
    c: Symmetric(g0,g2,g-1)
    c: DistanceX(g-3,g0) = 8
FEATURE [PartDesign::Pad] Pad002  label="screen"
  BaseFeature = -> Pad001
  Direction = (0,-1,-2e-16)
  Length = 0.3
  Length2 = 10
  Placement = pos=(0,0,0) rot=(1,0,0;1.5708rad)
  Profile = -> Sketch003
  ReferenceAxis = -> Sketch003 [N_Axis]
  Refine = true
  Type = 0
FEATURE [PartDesign::Pad] Pad003
  BaseFeature = -> Pad002
  Direction = (0,-1,-2e-16)
  Length = 1
  Length2 = 10
  Placement = pos=(0,0,0) rot=(1,0,0;1.5708rad)
  Profile = -> Sketch004
  ReferenceAxis = -> Sketch004 [N_Axis]
  Refine = true
  Type = 0
FEATURE [Sketcher::SketchObject] Sketch006
  ExternalGeometry = -> [Sketch003]
  FullyConstrained = false
  MapMode = 5
  Placement = pos=(0,0,0) rot=(1,0,0;1.5708rad)
  Support = -> [XZ_Plane001]
  sketch-geometry (3):
    g0: Circle CenterX=3.15 CenterY=2e-16 CenterZ=0 NormalX=0 NormalY=0 NormalZ=1 AngleXU=0 Radius=2.36505
    g1: LineSegment StartX=-51.65 StartY=30.8 StartZ=0 EndX=57.95 EndY=-30.8 EndZ=0
    g2: LineSegment StartX=-51.65 StartY=-30.8 StartZ=0 EndX=57.95 EndY=30.8 EndZ=0
  constraints (6):
    c: Coincident(g1,g-5)
    c: Coincident(g1,g-6)
    c: Coincident(g2,g-5)
    c: Coincident(g2,g-6)
    c: PointOnObject(g0,g2)
    c: PointOnObject(g0,g1)
FEATURE [PartDesign::Pad] Pad004  label="center_marker"
  BaseFeature = -> Pad003
  Direction = (0,-1,-2e-16)
  Length = 10
  Length2 = 10
  Placement = pos=(0,0,0) rot=(1,0,0;1.5708rad)
  Profile = -> Sketch006
  ReferenceAxis = -> Sketch006 [N_Axis]
  Refine = true
  Type = 0
FEATURE [PartDesign::Body] Body001  label="VoCore_5inch"
  Group = -> [Sketch002,Pad001,Sketch003,Pad002,Sketch004,Pad003,Sketch006,Pad004]
  Origin = -> Origin001
  Placement = pos=(3,-5,41) rot=(0,1,0;3.14159rad)
  Tip = -> Pad004
FEATURE [Sketcher::SketchObject] Sketch031
  FullyConstrained = false
  MapMode = 5
  Placement = pos=(0,0,0) rot=(1,0,0;1.5708rad)
  Support = -> [XZ_Plane]
  sketch-geometry (4):
    g0: ArcOfCircle CenterX=53.2019 CenterY=78.0947 CenterZ=0 NormalX=0 NormalY=0 NormalZ=1 AngleXU=0 Radius=4 StartAngle=1.5708 EndAngle=4.71239
    g1: ArcOfCircle CenterX=63.2019 CenterY=78.0947 CenterZ=0 NormalX=0 NormalY=0 NormalZ=1 AngleXU=0 Radius=4 StartAngle=4.71239 EndAngle=7.85398
    g2: LineSegment StartX=53.2019 StartY=74.0947 StartZ=0 EndX=63.2019 EndY=74.0947 EndZ=0
    g3: LineSegment StartX=63.2019 StartY=82.0947 StartZ=0 EndX=53.2019 EndY=82.0947 EndZ=0
  constraints (8):
    c: Tangent(g0,g2) = -1.5708
    c: Tangent(g2,g1) = -1.5708
    c: Tangent(g1,g3) = -1.5708
    c: Tangent(g3,g0) = -1.5708
    c: Equal(g0,g1)
    c: Horizontal(g2)
    c: Diameter(g0) = 8
    c: DistanceX(g3,g3) = 10
FEATURE [PartDesign::Pocket] Pocket015
  BaseFeature = -> Pocket014
  Direction = (0,1,2e-16)
  Length = 5
  Length2 = 5
  Placement = pos=(0,0,0) rot=(1,0,0;1.5708rad)
  Profile = -> Sketch031
  ReferenceAxis = -> Sketch031 [N_Axis]
  Refine = true
  Type = 1
FEATURE [PartDesign::Body] Body
  Group = -> [Sketch001,Sketch010,Sketch011,Pad,Sketch012,Sketch013,Sketch014,Sketch015,Pad012,Pocket007,Pocket008,Sketch023,Pocket009,Sketch024,Pad013,Sketch028,Pocket012,Sketch029,Pocket013,Sketch030,Pocket014,Sketch031,Pocket015]
  Origin = -> Origin
  Tip = -> Pocket015
FEATURE [PartDesign::Chamfer] Chamfer
  Angle = 45
  Base = -> Pocket010 [Edge436,Edge437,Edge434,Edge435]
  BaseFeature = -> Pocket010
  ChamferType = 1
  FlipDirection = false
  Placement = pos=(0,0,0) rot=(1,0,0;1.5708rad)
  Refine = true
  Size = 2
  Size2 = 0.5
  SupportTransform = false
  UseAllEdges = false
FEATURE [PartDesign::Pocket] Pocket011  label="front_magnet_cutouts"
  BaseFeature = -> Chamfer
  Direction = (0,1,2e-16)
  Length = 1.5
  Length2 = 5
  Placement = pos=(0,0,0) rot=(1,0,0;1.5708rad)
  Profile = -> Sketch027
  ReferenceAxis = -> Sketch027 [N_Axis]
  Refine = true
  Type = 0
FEATURE [PartDesign::Body] Body002  label="front"
  Group = -> [Sketch005,Sketch007,Pad005,Sketch008,Pad006,Pocket,Sketch009,Pocket001,Sketch,Sketch016,Pocket004,Mirrored,Sketch017,Pocket005,Sketch018,Mirrored001,Pocket006,Mirrored002,Sketch025,Pad014,Sketch026,Pocket010,Chamfer,Sketch027,Pocket011]
  Origin = -> Origin002
  Placement = pos=(0,-88,0) rot=(0,0,1;3.14159rad)
  Tip = -> Pocket011
FEATURE [Sketcher::SketchObject] Sketch034
  FullyConstrained = true
  MapMode = 5
  Placement = pos=(0,0,0) rot=(1,0,0;1.5708rad)
  Support = -> [XZ_Plane006]
  sketch-geometry (2):
    g0: Circle CenterX=0 CenterY=0 CenterZ=0 NormalX=0 NormalY=0 NormalZ=1 AngleXU=0 Radius=150
    g1: Circle CenterX=0 CenterY=0 CenterZ=0 NormalX=0 NormalY=0 NormalZ=1 AngleXU=0 Radius=135
  constraints (4):
    c: Coincident(g0,g-1)
    c: Diameter(g0) = 300
    c: Coincident(g1,g0)
    c: Diameter(g1) = 270
FEATURE [PartDesign::Pad] Pad016
  Direction = (0,-1,2e-16)
  Length = 30
  Length2 = 10
  Placement = pos=(0,0,0) rot=(1,0,0;1.5708rad)
  Profile = -> Sketch034
  ReferenceAxis = -> Sketch034 [N_Axis]
  Refine = true
  Type = 0
FEATURE [PartDesign::Body] Body006  label="Wheel"
  Group = -> [Sketch034,Pad016]
  Origin = -> Origin006
  Placement = pos=(0,-84,-35) rot=(0,0,1;0rad)
  Tip = -> Pad016
FEATURE [Sketcher::SketchObject] Sketch036  label="sk_mount_plate002"
  AttachmentOffset = pos=(0,14,0) rot=(0,0,1;0rad)
  FullyConstrained = true
  MapMode = 5
  Placement = pos=(0,-3.1e-15,14) rot=(1,0,0;1.5708rad)
  Support = -> [XZ_Plane007]
  sketch-geometry (14):
    g0: Circle CenterX=-28 CenterY=0 CenterZ=0 NormalX=0 NormalY=0 NormalZ=1 AngleXU=0 Radius=3
    g1: Circle CenterX=28 CenterY=0 CenterZ=0 NormalX=0 NormalY=0 NormalZ=1 AngleXU=0 Radius=3
    g2: Circle CenterX=-50 CenterY=0 CenterZ=0 NormalX=0 NormalY=0 NormalZ=1 AngleXU=0 Radius=5
    g3: Circle CenterX=50 CenterY=0 CenterZ=0 NormalX=0 NormalY=0 NormalZ=1 AngleXU=0 Radius=5
    g4: LineSegment StartX=-50 StartY=0 StartZ=0 EndX=50 EndY=0 EndZ=0
    g5: ArcOfCircle CenterX=1.69e-14 CenterY=-69 CenterZ=0 NormalX=0 NormalY=0 NormalZ=1 AngleXU=0 Radius=100 StartAngle=1.21654 EndAngle=1.92505
    g6: ArcOfCircle CenterX=106.026 CenterY=217.668 CenterZ=0 NormalX=0 NormalY=0 NormalZ=1 AngleXU=0 Radius=205.647 StartAngle=4.35814 EndAngle=4.64413
    g7: GeomPoint X=0 Y=31 Z=0
    g8: LineSegment StartX=28 StartY=0 StartZ=0 EndX=28 EndY=27 EndZ=0
    g9: LineSegment StartX=50 StartY=0 StartZ=0 EndX=50 EndY=19.8 EndZ=0
    g10: ArcOfCircle CenterX=-106.026 CenterY=217.668 CenterZ=0 NormalX=0 NormalY=0 NormalZ=1 AngleXU=0 Radius=205.647 StartAngle=4.78065 EndAngle=5.06664
    g11: LineSegment StartX=-50 StartY=0 StartZ=0 EndX=-50 EndY=19.8 EndZ=0
    g12: LineSegment StartX=-92 StartY=12.5 StartZ=0 EndX=-92 EndY=0 EndZ=0
    g13: LineSegment StartX=92 StartY=12.5 StartZ=0 EndX=92 EndY=0 EndZ=0
  constraints (39):
    c: DistanceX(g0,g1) = 56  'mount_holes_distance'
    c: Symmetric(g0,g1,g-2)
    c: Equal(g0,g1)
    c: Diameter(g0) = 6  'mount_holes_diameter'
    c: Equal(g2,g3)
    c: Diameter(g2) = 10  'motor_mount_holes_diameter'
    c: Symmetric(g2,g3,g-2)
    c: Coincident(g4,g2)
    c: Coincident(g4,g3)
    c: PointOnObject(g0,g4)
    c: PointOnObject(g-1,g4)
    c: Symmetric(g5,g5,g-2)
    c: Coincident(g6,g5)
    c: PointOnObject(g7,g5)
    c: PointOnObject(g7,g-2)
    c: DistanceY(g-1,g7) = 31
    c: Coincident(g8,g1)
    c: PointOnObject(g8,g5)
    c: Vertical(g8)
    c: Coincident(g9,g3)
    c: PointOnObject(g9,g6)
    c: Vertical(g9)
    c: DistanceY(g1,g8) = 27
    c: DistanceX(g2,g3) = 100
    c: DistanceY(g9,g9) = 19.8
    c: Coincident(g11,g2)
    c: PointOnObject(g11,g10)
    c: Vertical(g11)
    c: DistanceY(g11,g11) = 19.8
    c: Symmetric(g6,g10,g-2)
    c: Coincident(g12,g10)
    c: PointOnObject(g12,g-1)
    c: Vertical(g12)
    c: DistanceY(g12,g12) = 12.5
    c: DistanceX(g12,g-1) = 92
    c: Tangent(g10,g5) = 1.5708
    c: Coincident(g13,g6)
    c: PointOnObject(g13,g-1)
    c: Vertical(g13)
FEATURE [Sketcher::SketchObject] Sketch037
  ExternalGeometry = -> [Sketch036]
  FullyConstrained = false
  MapMode = 5
  Placement = pos=(0,0,0) rot=(1,0,0;1.5708rad)
  Support = -> [XZ_Plane007]
  sketch-geometry (19):
    g0: LineSegment StartX=-74.1374 StartY=12.9048 StartZ=0 EndX=-74.1374 EndY=35.0983 EndZ=0
    g1: LineSegment StartX=86.4714 StartY=40.0983 StartZ=0 EndX=86.4714 EndY=91.2347 EndZ=0
    g2: ArcOfCircle CenterX=-86.4323 CenterY=296.882 CenterZ=0 NormalX=0 NormalY=0 NormalZ=1 AngleXU=0 Radius=205.647 StartAngle=4.7122 EndAngle=4.96674
    g3: ArcOfCircle CenterX=86.4323 CenterY=296.882 CenterZ=0 NormalX=0 NormalY=0 NormalZ=1 AngleXU=0 Radius=205.647 StartAngle=4.45804 EndAngle=4.71258
    g4: LineSegment StartX=-34.689 StartY=97.8508 StartZ=0 EndX=-34.689 EndY=38.7906 EndZ=0
    g5: ArcOfCircle CenterX=-5.9e-15 CenterY=4.06019 CenterZ=0 NormalX=0 NormalY=0 NormalZ=1 AngleXU=0 Radius=100 StartAngle=1.21654 EndAngle=1.92505
    g6: LineSegment StartX=-86.4714 StartY=91.2347 StartZ=0 EndX=-86.4714 EndY=40.0983 EndZ=0
    g7: LineSegment StartX=-81.4714 StartY=35.0983 StartZ=0 EndX=-74.1374 EndY=35.0983 EndZ=0
    g8: LineSegment StartX=81.4714 StartY=35.0983 StartZ=0 EndX=74.1374 EndY=35.0983 EndZ=0
    g9: LineSegment StartX=74.1374 StartY=35.0983 StartZ=0 EndX=74.1374 EndY=12.9048 EndZ=0
    g10: ArcOfCircle CenterX=-81.4714 CenterY=40.0983 CenterZ=0 NormalX=0 NormalY=0 NormalZ=1 AngleXU=0 Radius=5 StartAngle=3.14159 EndAngle=4.71239
    g11: ArcOfCircle CenterX=81.4714 CenterY=40.0983 CenterZ=0 NormalX=0 NormalY=0 NormalZ=1 AngleXU=0 Radius=5 StartAngle=4.71239 EndAngle=6.28319
    g12: Circle CenterX=50 CenterY=14 CenterZ=0 NormalX=0 NormalY=0 NormalZ=1 AngleXU=0 Radius=5
    g13: Circle CenterX=28 CenterY=14 CenterZ=0 NormalX=0 NormalY=0 NormalZ=1 AngleXU=0 Radius=3
    g14: Circle CenterX=-28 CenterY=14 CenterZ=0 NormalX=0 NormalY=0 NormalZ=1 AngleXU=0 Radius=3
    g15: Circle CenterX=-50 CenterY=14 CenterZ=0 NormalX=0 NormalY=0 NormalZ=1 AngleXU=0 Radius=5
    g16: LineSegment StartX=-66.2726 StartY=5.0399 StartZ=0 EndX=66.2726 EndY=5.0399 EndZ=0
    g17: ArcOfCircle CenterX=-66.2726 CenterY=12.9048 CenterZ=0 NormalX=0 NormalY=0 NormalZ=1 AngleXU=0 Radius=7.86486 StartAngle=3.14159 EndAngle=4.71239
    g18: ArcOfCircle CenterX=66.2726 CenterY=12.9048 CenterZ=0 NormalX=0 NormalY=0 NormalZ=1 AngleXU=0 Radius=7.86486 StartAngle=4.71239 EndAngle=6.28319
  constraints (40):
    c: Vertical(g0)
    c: Equal(g2,g-3)
    c: Coincident(g3,g1)
    c: Equal(g3,g-5)
    c: Coincident(g4,g2)
    c: Coincident(g4,g-4)
    c: Vertical(g4)
    c: Symmetric(g2,g3,g-2)
    c: Coincident(g5,g2)
    c: Coincident(g5,g3)
    c: Equal(g5,g-4)
    c: Coincident(g6,g2)
    c: Vertical(g6)
    c: Horizontal(g7)
    c: Coincident(g0,g7)
    c: Symmetric(g2,g1,g-2)
    c: Coincident(g9,g8)
    c: Vertical(g9)
    c: Symmetric(g8,g0,g-2)
    c: Tangent(g6,g10) = -1.5708
    c: Tangent(g7,g10) = -1.5708
    c: Tangent(g8,g11) = 1.5708
    c: Tangent(g1,g11) = -1.5708
    c: Equal(g10,g11)
    c: Horizontal(g8)
    c: Vertical(g1)
    c: Radius(g10) = 5
    c: Coincident(g12,g-9)
    c: Coincident(g13,g-8)
    c: Coincident(g14,g-7)
    c: Coincident(g15,g-6)
    c: Equal(g15,g-6)
    c: Equal(g14,g-7)
    c: Equal(g13,g-8)
    c: Equal(g12,g-9)
    c: Tangent(g0,g17) = 1.5708
    c: Tangent(g16,g17) = -1.5708
    c: Tangent(g9,g18) = 1.5708
    c: Tangent(g16,g18) = -1.5708
    c: Symmetric(g16,g16,g-2)
FEATURE [Sketcher::SketchObject] Sketch038
  FullyConstrained = false
  MapMode = 5
  Placement = pos=(0,0,0) rot=(1,0,0;1.5708rad)
  Support = -> [XZ_Plane007]
  sketch-geometry (14):
    g0: ArcOfCircle CenterX=-85.489 CenterY=295.581 CenterZ=0 NormalX=0 NormalY=0 NormalZ=1 AngleXU=0 Radius=204.723 StartAngle=4.70521 EndAngle=4.95424
    g1: ArcOfCircle CenterX=9e-16 CenterY=5.35596 CenterZ=0 NormalX=0 NormalY=0 NormalZ=1 AngleXU=0 Radius=98.4585 StartAngle=1.19149 EndAngle=1.95011
    g2: ArcOfCircle CenterX=85.489 CenterY=295.581 CenterZ=0 NormalX=0 NormalY=0 NormalZ=1 AngleXU=0 Radius=204.723 StartAngle=4.47054 EndAngle=4.71957
    g3: LineSegment StartX=86.9591 StartY=90.863 StartZ=0 EndX=86.9591 EndY=41.4311 EndZ=0
    g4: LineSegment StartX=80.8247 StartY=35.2968 StartZ=0 EndX=73.6598 EndY=35.2968 EndZ=0
    g5: LineSegment StartX=-73.6598 StartY=35.2968 StartZ=0 EndX=-80.8247 EndY=35.2968 EndZ=0
    g6: LineSegment StartX=-86.9591 StartY=41.4311 StartZ=0 EndX=-86.9591 EndY=90.863 EndZ=0
    g7: ArcOfCircle CenterX=80.8247 CenterY=41.4311 CenterZ=0 NormalX=0 NormalY=0 NormalZ=1 AngleXU=0 Radius=6.13437 StartAngle=4.71239 EndAngle=6.28319
    g8: ArcOfCircle CenterX=-80.8247 CenterY=41.4311 CenterZ=0 NormalX=0 NormalY=0 NormalZ=1 AngleXU=0 Radius=6.13437 StartAngle=3.14159 EndAngle=4.71239
    g9: LineSegment StartX=-73.6598 StartY=35.2968 StartZ=0 EndX=-73.6598 EndY=29.9833 EndZ=0
    g10: LineSegment StartX=73.6598 StartY=35.2968 StartZ=0 EndX=73.6598 EndY=29.9833 EndZ=0
    g11: ArcOfCircle CenterX=-106.712 CenterY=232.036 CenterZ=0 NormalX=0 NormalY=0 NormalZ=1 AngleXU=0 Radius=204.738 StartAngle=4.87454 EndAngle=5.06707
    g12: ArcOfCircle CenterX=4e-16 CenterY=-55.4945 CenterZ=0 NormalX=0 NormalY=0 NormalZ=1 AngleXU=0 Radius=101.956 StartAngle=1.21402 EndAngle=1.92758
    g13: ArcOfCircle CenterX=106.894 CenterY=232.721 CenterZ=0 NormalX=0 NormalY=0 NormalZ=1 AngleXU=0 Radius=205.444 StartAngle=4.35804 EndAngle=4.54991
  constraints (25):
    c: Coincident(g1,g0)
    c: Coincident(g2,g1)
    c: Coincident(g3,g2)
    c: Coincident(g6,g0)
    c: Coincident(g7,g4)
    c: Coincident(g10,g4)
    c: Vertical(g10)
    c: Coincident(g11,g9)
    c: Coincident(g12,g11)
    c: Coincident(g13,g12)
    c: Coincident(g13,g10)
    c: Equal(g2,g0)
    c: Symmetric(g0,g2,g-2)
    c: Vertical(g6)
    c: Symmetric(g3,g6,g-2)
    c: Symmetric(g9,g10,g-2)
    c: Symmetric(g9,g4,g-2)
    c: Symmetric(g0,g1,g-2)
    c: Tangent(g8,g6) = 1.5708
    c: Tangent(g7,g3) = 1.5708
    c: Symmetric(g4,g5,g-2)
    c: Symmetric(g11,g12,g-2)
    c: Coincident(g5,g9)
    c: Tangent(g8,g5) = 1.5708
    c: Horizontal(g5)
FEATURE [PartDesign::Pad] Pad019
  Direction = (0,-1,-2e-16)
  Length = 7
  Length2 = 10
  Placement = pos=(0,0,0) rot=(1,0,0;1.5708rad)
  Profile = -> Sketch037
  ReferenceAxis = -> Sketch037 [N_Axis]
  Refine = true
  Type = 0
FEATURE [PartDesign::Pad] Pad020
  BaseFeature = -> Pad019
  Direction = (0,-1,-2e-16)
  Length = 50
  Length2 = 10
  Placement = pos=(0,0,0) rot=(1,0,0;1.5708rad)
  Profile = -> Sketch038
  ReferenceAxis = -> Sketch038 [N_Axis]
  Refine = true
  Reversed = true
  Type = 0
FEATURE [Sketcher::SketchObject] Sketch041
  AttachmentOffset = pos=(0,0,7) rot=(0,0,1;0rad)
  ExternalGeometry = -> [Sketch038]
  FullyConstrained = false
  MapMode = 5
  Placement = pos=(0,-7,-1.6e-15) rot=(1,0,0;1.5708rad)
  Support = -> [XZ_Plane007]
  sketch-geometry (12):
    g0: LineSegment StartX=-82.3806 StartY=87.705 StartZ=0 EndX=-82.3806 EndY=41.8091 EndZ=0
    g1: LineSegment StartX=-82.3806 StartY=41.8091 StartZ=0 EndX=-70.9672 EndY=41.8091 EndZ=0
    g2: LineSegment StartX=82.3806 StartY=87.705 StartZ=0 EndX=82.3806 EndY=41.8091 EndZ=0
    g3: LineSegment StartX=82.3806 StartY=41.8091 StartZ=0 EndX=70.9672 EndY=41.8091 EndZ=0
    g4: LineSegment StartX=70.9672 StartY=41.8091 StartZ=0 EndX=70.9672 EndY=33.3843 EndZ=0
    g5: LineSegment StartX=-70.9672 StartY=41.8091 StartZ=0 EndX=-70.9672 EndY=33.3843 EndZ=0
    g6: ArcOfCircle CenterX=-110.461 CenterY=229.567 CenterZ=0 NormalX=0 NormalY=0 NormalZ=1 AngleXU=0 Radius=200.119 StartAngle=4.91105 EndAngle=5.08675
    g7: ArcOfCircle CenterX=-5.8e-15 CenterY=-51.5867 CenterZ=0 NormalX=0 NormalY=0 NormalZ=1 AngleXU=0 Radius=101.956 StartAngle=1.19644 EndAngle=1.94515
    g8: ArcOfCircle CenterX=111.972 CenterY=234.694 CenterZ=0 NormalX=0 NormalY=0 NormalZ=1 AngleXU=0 Radius=205.444 StartAngle=4.34031 EndAngle=4.51145
    g9: ArcOfCircle CenterX=-80.8734 CenterY=292.423 CenterZ=0 NormalX=0 NormalY=0 NormalZ=1 AngleXU=0 Radius=204.723 StartAngle=4.70503 EndAngle=4.98241
    g10: ArcOfCircle CenterX=6.4e-15 CenterY=0.22645 CenterZ=0 NormalX=0 NormalY=0 NormalZ=1 AngleXU=0 Radius=98.4585 StartAngle=1.30078 EndAngle=1.84081
    g11: ArcOfCircle CenterX=80.8734 CenterY=292.423 CenterZ=0 NormalX=0 NormalY=0 NormalZ=1 AngleXU=0 Radius=204.723 StartAngle=4.44237 EndAngle=4.71975
  constraints (26):
    c: Vertical(g0)
    c: Coincident(g1,g0)
    c: Horizontal(g1)
    c: Coincident(g3,g2)
    c: Coincident(g4,g3)
    c: Vertical(g4)
    c: Coincident(g5,g1)
    c: Coincident(g6,g5)
    c: Coincident(g8,g4)
    c: Coincident(g8,g7)
    c: Symmetric(g0,g2,g-2)
    c: Symmetric(g2,g0,g-2)
    c: Symmetric(g1,g3,g-2)
    c: Symmetric(g6,g7,g-2)
    c: Symmetric(g5,g4,g-2)
    c: Coincident(g9,g0)
    c: Coincident(g10,g9)
    c: Coincident(g11,g2)
    c: Symmetric(g9,g10,g-2)
    c: Equal(g8,g-8)
    c: Equal(g-4,g7)
    c: Tangent(g7,g6) = 1.5708
    c: Equal(g10,g-3)
    c: Equal(g9,g-6)
    c: Equal(g11,g-5)
    c: Tangent(g11,g10) = 1.5708
FEATURE [PartDesign::Pocket] Pocket019
  BaseFeature = -> Pad020
  Direction = (0,1,2e-16)
  Length = 52
  Length2 = 5
  Placement = pos=(0,0,0) rot=(1,0,0;1.5708rad)
  Profile = -> Sketch041
  ReferenceAxis = -> Sketch041 [N_Axis]
  Refine = true
  Type = 0
FEATURE [Sketcher::SketchObject] Sketch043
  FullyConstrained = false
  MapMode = 5
  Placement = pos=(0,0,0) rot=(1,0,0;1.5708rad)
  Support = -> [XZ_Plane008]
  sketch-geometry (21):
    g0: LineSegment StartX=272.354 StartY=37.4294 StartZ=0 EndX=272.344 EndY=-21.7954 EndZ=0
    g1: LineSegment StartX=182.404 StartY=-108.908 StartZ=0 EndX=105.813 EndY=-108.908 EndZ=0
    g2: LineSegment StartX=267.374 StartY=-26.7942 StartZ=0 EndX=208.289 EndY=-27.1442 EndZ=0
    g3: LineSegment StartX=203.514 StartY=-31.324 StartZ=0 EndX=194.119 EndY=-98.7128 EndZ=0
    g4: LineSegment StartX=74.7381 StartY=34.5363 StartZ=0 EndX=81.5483 EndY=34.5792 EndZ=0
    g5: LineSegment StartX=87.5384 StartY=40.6059 StartZ=0 EndX=87.5495 EndY=90.99 EndZ=0
    g6: ArcOfCircle CenterX=81.5103 CenterY=40.6072 CenterZ=0 NormalX=0 NormalY=0 NormalZ=1 AngleXU=0 Radius=6.02816 StartAngle=4.71869 EndAngle=6.28297
    g7: ArcOfCircle CenterX=182.404 CenterY=-97.0795 CenterZ=0 NormalX=0 NormalY=0 NormalZ=1 AngleXU=0 Radius=11.8281 StartAngle=4.71239 EndAngle=6.14466
    g8: ArcOfCircle CenterX=208.317 CenterY=-31.9936 CenterZ=0 NormalX=0 NormalY=0 NormalZ=1 AngleXU=0 Radius=4.84955 StartAngle=1.57672 EndAngle=3.00306
    g9: ArcOfCircle CenterX=267.344 CenterY=-21.7946 CenterZ=0 NormalX=0 NormalY=0 NormalZ=1 AngleXU=0 Radius=4.99975 StartAngle=4.71831 EndAngle=6.28301
    g10: LineSegment StartX=74.7381 StartY=34.5363 StartZ=0 EndX=74.7381 EndY=9.5079 EndZ=0
    g11: ArcOfCircle CenterX=267.354 CenterY=37.4293 CenterZ=0 NormalX=0 NormalY=0 NormalZ=1 AngleXU=0 Radius=5.00007 StartAngle=1.79458e-05 EndAngle=1.04037
    g12: ArcOfCircle CenterX=88.573 CenterY=-267.38 CenterZ=0 NormalX=0 NormalY=0 NormalZ=1 AngleXU=0 Radius=358.372 StartAngle=1.04034 EndAngle=1.57365
    g13: Circle CenterX=87.2657 CenterY=19.2814 CenterZ=0 NormalX=0 NormalY=0 NormalZ=1 AngleXU=0 Radius=3.5
    g14: Circle CenterX=108.66 CenterY=-98.6934 CenterZ=0 NormalX=0 NormalY=0 NormalZ=1 AngleXU=0 Radius=3.5
    g15: LineSegment StartX=74.7381 StartY=9.5079 StartZ=0 EndX=115.533 EndY=9.5079 EndZ=0
    g16: ArcOfCircle CenterX=79.1289 CenterY=-29.4223 CenterZ=0 NormalX=0 NormalY=0 NormalZ=1 AngleXU=0 Radius=60.7241 StartAngle=5.81384 EndAngle=6.77511
    g17: ArcOfCircle CenterX=115.533 CenterY=-9.91453 CenterZ=0 NormalX=0 NormalY=0 NormalZ=1 AngleXU=0 Radius=19.4224 StartAngle=0.491924 EndAngle=1.5708
    g18: ArcOfCircle CenterX=105.813 CenterY=-99.1606 CenterZ=0 NormalX=0 NormalY=0 NormalZ=1 AngleXU=0 Radius=9.74695 StartAngle=2.10855 EndAngle=4.71239
    g19: ArcOfCircle CenterX=65.411 CenterY=-25.694 CenterZ=0 NormalX=0 NormalY=0 NormalZ=1 AngleXU=0 Radius=74.7005 StartAngle=5.58707 EndAngle=5.85239
    g20: ArcOfCircle CenterX=44.7737 CenterY=3.19022 CenterZ=0 NormalX=0 NormalY=0 NormalZ=1 AngleXU=0 Radius=109.423 StartAngle=5.25014 EndAngle=5.50537
  constraints (23):
    c: Tangent(g4,g6) = -1.5708
    c: Tangent(g5,g6) = -1.5708
    c: Tangent(g3,g7) = 1.5708
    c: Tangent(g3,g8) = -1.5708
    c: Tangent(g2,g8) = -1.5708
    c: Tangent(g2,g9) = 1.5708
    c: Tangent(g0,g9) = 1.5708
    c: Coincident(g10,g4)
    c: Coincident(g11,g0)
    c: Coincident(g12,g5)
    c: Coincident(g12,g11)
    c: Equal(g13,g14)
    c: Horizontal(g1)
    c: Vertical(g10)
    c: Horizontal(g15)
    c: Tangent(g15,g17) = 1.5708
    c: Tangent(g16,g17) = -1.5708
    c: Coincident(g19,g16)
    c: Coincident(g20,g19)
    c: Tangent(g7,g1) = 1.5708
    c: Tangent(g18,g1) = 1.5708
    c: Tangent(g20,g18) = 1.5708
    c: Coincident(g15,g10)
FEATURE [Sketcher::SketchObject] MirroredSketch
  FullyConstrained = false
  Placement = pos=(0,0,0) rot=(1,0,0;1.5708rad)
  sketch-geometry (21):
    g0: LineSegment StartX=-272.354 StartY=37.4294 StartZ=0 EndX=-272.344 EndY=-21.7954 EndZ=0
    g1: LineSegment StartX=-182.404 StartY=-108.908 StartZ=0 EndX=-105.813 EndY=-108.908 EndZ=0
    g2: LineSegment StartX=-267.374 StartY=-26.7942 StartZ=0 EndX=-208.289 EndY=-27.1442 EndZ=0
    g3: LineSegment StartX=-203.514 StartY=-31.324 StartZ=0 EndX=-194.119 EndY=-98.7128 EndZ=0
    g4: LineSegment StartX=-74.7381 StartY=34.5363 StartZ=0 EndX=-81.5483 EndY=34.5792 EndZ=0
    g5: LineSegment StartX=-87.5384 StartY=40.6059 StartZ=0 EndX=-87.5495 EndY=90.99 EndZ=0
    g6: ArcOfCircle CenterX=-81.5103 CenterY=40.6072 CenterZ=0 NormalX=0 NormalY=0 NormalZ=1 AngleXU=0 Radius=6.02816 StartAngle=3.14181 EndAngle=4.70609
    g7: ArcOfCircle CenterX=-182.404 CenterY=-97.0795 CenterZ=0 NormalX=0 NormalY=0 NormalZ=1 AngleXU=0 Radius=11.8281 StartAngle=3.28012 EndAngle=4.71239
    g8: ArcOfCircle CenterX=-208.317 CenterY=-31.9936 CenterZ=0 NormalX=0 NormalY=0 NormalZ=1 AngleXU=0 Radius=4.84955 StartAngle=0.13853 EndAngle=1.56487
    g9: ArcOfCircle CenterX=-267.344 CenterY=-21.7946 CenterZ=0 NormalX=0 NormalY=0 NormalZ=1 AngleXU=0 Radius=4.99975 StartAngle=3.14177 EndAngle=4.70647
    g10: LineSegment StartX=-74.7381 StartY=34.5363 StartZ=0 EndX=-74.7381 EndY=9.5079 EndZ=0
    g11: ArcOfCircle CenterX=-267.354 CenterY=37.4293 CenterZ=0 NormalX=0 NormalY=0 NormalZ=1 AngleXU=0 Radius=5.00007 StartAngle=2.10123 EndAngle=3.14157
    g12: ArcOfCircle CenterX=-88.573 CenterY=-267.38 CenterZ=0 NormalX=0 NormalY=0 NormalZ=1 AngleXU=0 Radius=358.372 StartAngle=1.56794 EndAngle=2.10125
    g13: Circle CenterX=-87.2657 CenterY=19.2814 CenterZ=0 NormalX=0 NormalY=0 NormalZ=1 AngleXU=0 Radius=3.5
    g14: Circle CenterX=-108.66 CenterY=-98.6934 CenterZ=0 NormalX=0 NormalY=0 NormalZ=1 AngleXU=0 Radius=3.5
    g15: LineSegment StartX=-74.7381 StartY=9.5079 StartZ=0 EndX=-115.533 EndY=9.5079 EndZ=0
    g16: ArcOfCircle CenterX=-79.1289 CenterY=-29.4223 CenterZ=0 NormalX=0 NormalY=0 NormalZ=1 AngleXU=0 Radius=60.7241 StartAngle=2.64967 EndAngle=3.61094
    g17: ArcOfCircle CenterX=-115.533 CenterY=-9.91453 CenterZ=0 NormalX=0 NormalY=0 NormalZ=1 AngleXU=0 Radius=19.4224 StartAngle=1.5708 EndAngle=2.64967
    g18: ArcOfCircle CenterX=-105.813 CenterY=-99.1606 CenterZ=0 NormalX=0 NormalY=0 NormalZ=1 AngleXU=0 Radius=9.74695 StartAngle=4.71239 EndAngle=7.31623
    g19: ArcOfCircle CenterX=-65.411 CenterY=-25.694 CenterZ=0 NormalX=0 NormalY=0 NormalZ=1 AngleXU=0 Radius=74.7005 StartAngle=3.57238 EndAngle=3.83771
    g20: ArcOfCircle CenterX=-44.7737 CenterY=3.19022 CenterZ=0 NormalX=0 NormalY=0 NormalZ=1 AngleXU=0 Radius=109.423 StartAngle=3.91941 EndAngle=4.17464
  constraints (23):
    c: Tangent(g4,g6) = 1.5708
    c: Tangent(g5,g6) = 1.5708
    c: Tangent(g3,g7) = -1.5708
    c: Tangent(g3,g8) = 1.5708
    c: Tangent(g2,g8) = 1.5708
    c: Tangent(g2,g9) = -1.5708
    c: Tangent(g0,g9) = -1.5708
    c: Coincident(g10,g4)
    c: Coincident(g11,g0)
    c: Coincident(g12,g5)
    c: Coincident(g12,g11)
    c: Equal(g13,g14)
    c: Horizontal(g1)
    c: Vertical(g10)
    c: Horizontal(g15)
    c: Tangent(g15,g17) = -1.5708
    c: Tangent(g16,g17) = -1.5708
    c: Coincident(g19,g16)
    c: Coincident(g20,g19)
    c: Tangent(g7,g1) = -1.5708
    c: Tangent(g18,g1) = -1.5708
    c: Tangent(g20,g18) = 1.5708
    c: Coincident(g15,g10)
FEATURE [PartDesign::Pad] Pad021
  Direction = (0,-1,-2e-16)
  Length = 7
  Length2 = 10
  Placement = pos=(0,0,0) rot=(1,0,0;1.5708rad)
  Profile = -> Sketch043
  ReferenceAxis = -> Sketch043 [N_Axis]
  Refine = true
  Type = 0
FEATURE [PartDesign::Pad] Pad022
  Direction = (0,-1,0)
  Length = 7
  Length2 = 10
  Placement = pos=(0,0,0) rot=(1,0,0;1.5708rad)
  Profile = -> MirroredSketch
  ReferenceAxis = -> MirroredSketch [N_Axis]
  Refine = true
  Type = 0
FEATURE [Sketcher::SketchObject] Sketch044
  AttachmentOffset = pos=(0,0,7) rot=(0,0,1;0rad)
  ExternalGeometry = -> [Sketch043]
  FullyConstrained = false
  MapMode = 5
  Placement = pos=(0,-7,-1.6e-15) rot=(1,0,0;1.5708rad)
  Support = -> [XZ_Plane008]
  sketch-geometry (27):
    g0: Circle CenterX=211.699 CenterY=15.68 CenterZ=0 NormalX=0 NormalY=0 NormalZ=1 AngleXU=0 Radius=7.9
    g1: Circle CenterX=211.699 CenterY=-9.39693 CenterZ=0 NormalX=0 NormalY=0 NormalZ=1 AngleXU=0 Radius=7.9
    g2: Circle CenterX=238.467 CenterY=15.68 CenterZ=0 NormalX=0 NormalY=0 NormalZ=1 AngleXU=0 Radius=7.9
    g3: Circle CenterX=238.467 CenterY=-9.39693 CenterZ=0 NormalX=0 NormalY=0 NormalZ=1 AngleXU=0 Radius=7.9
    g4: LineSegment StartX=211.699 StartY=15.68 StartZ=0 EndX=238.467 EndY=15.68 EndZ=0
    g5: LineSegment StartX=238.467 StartY=-9.39693 StartZ=0 EndX=211.699 EndY=-9.39693 EndZ=0
    g6: Circle CenterX=211.699 CenterY=40.757 CenterZ=0 NormalX=0 NormalY=0 NormalZ=1 AngleXU=0 Radius=7.9
    g7: Circle CenterX=238.467 CenterY=40.757 CenterZ=0 NormalX=0 NormalY=0 NormalZ=1 AngleXU=0 Radius=7.9
    g8: LineSegment StartX=211.699 StartY=40.757 StartZ=0 EndX=238.467 EndY=40.757 EndZ=0
    g9: LineSegment StartX=211.699 StartY=-9.39693 StartZ=0 EndX=211.699 EndY=15.68 EndZ=0
    g10: LineSegment StartX=211.699 StartY=15.68 StartZ=0 EndX=211.699 EndY=40.757 EndZ=0
    g11: Circle CenterX=180.86 CenterY=-25.593 CenterZ=0 NormalX=0 NormalY=0 NormalZ=1 AngleXU=0 Radius=7.9
    g12: Circle CenterX=177.028 CenterY=-60.1553 CenterZ=0 NormalX=0 NormalY=0 NormalZ=1 AngleXU=0 Radius=7.9
    g13: Circle CenterX=163.778 CenterY=-92.3061 CenterZ=0 NormalX=0 NormalY=0 NormalZ=1 AngleXU=0 Radius=7.9
    g14: Circle CenterX=174.975 CenterY=8.67946 CenterZ=0 NormalX=0 NormalY=0 NormalZ=1 AngleXU=0 Radius=7.9
    g15: ArcOfCircle CenterX=56.5275 CenterY=-29.3007 CenterZ=0 NormalX=0 NormalY=0 NormalZ=1 AngleXU=0 Radius=124.388 StartAngle=5.75204 EndAngle=6.59348
    g16: LineSegment StartX=174.975 StartY=8.67946 StartZ=0 EndX=180.86 EndY=-25.593 EndZ=0
    g17: LineSegment StartX=180.86 StartY=-25.593 StartZ=0 EndX=177.028 EndY=-60.1553 EndZ=0
    g18: LineSegment StartX=177.028 StartY=-60.1553 StartZ=0 EndX=163.778 EndY=-92.3061 EndZ=0
    g19: Circle CenterX=116.789 CenterY=72.7511 CenterZ=0 NormalX=0 NormalY=0 NormalZ=1 AngleXU=0 Radius=8.25
    g20: Circle CenterX=146.797 CenterY=68.9164 CenterZ=0 NormalX=0 NormalY=0 NormalZ=1 AngleXU=0 Radius=8.25
    g21: LineSegment StartX=116.789 StartY=72.7511 StartZ=0 EndX=118.2 EndY=89.7647 EndZ=0
    g22: LineSegment StartX=146.797 StartY=68.9164 StartZ=0 EndX=149.709 EndY=85.7383 EndZ=0
    g23: LineSegment StartX=184.477 StartY=77.9208 StartZ=0 EndX=176.436 EndY=62.8607 EndZ=0
    g24: Circle CenterX=176.436 CenterY=62.8607 CenterZ=0 NormalX=0 NormalY=0 NormalZ=1 AngleXU=0 Radius=8.25
    g25: LineSegment StartX=116.789 StartY=72.7511 StartZ=0 EndX=146.797 EndY=68.9164 EndZ=0
    g26: LineSegment StartX=146.797 StartY=68.9164 StartZ=0 EndX=176.436 EndY=62.8607 EndZ=0
  constraints (56):
    c: Diameter(g0) = 15.8
    c: Coincident(g4,g0)
    c: Coincident(g4,g2)
    c: Coincident(g5,g3)
    c: Coincident(g5,g1)
    c: Equal(g5,g4)
    c: Coincident(g8,g6)
    c: Coincident(g8,g7)
    c: Equal(g8,g5)
    c: Equal(g6,g0)
    c: Equal(g0,g1)
    c: Equal(g1,g3)
    c: Equal(g3,g2)
    c: Equal(g2,g7)
    c: Coincident(g9,g1)
    c: Coincident(g9,g0)
    c: Coincident(g10,g0)
    c: Coincident(g10,g6)
    c: Equal(g9,g10)
    c: Parallel(g9,g10)
    c: Perpendicular(g9,g5)
    c: Equal(g13,g12)
    c: Equal(g12,g11)
    c: Equal(g11,g14)
    c: Coincident(g15,g13)
    c: PointOnObject(g11,g15)
    c: PointOnObject(g12,g15)
    c: Coincident(g16,g14)
    c: Coincident(g16,g11)
    c: Coincident(g17,g11)
    c: Coincident(g17,g12)
    c: Coincident(g18,g12)
    c: Coincident(g18,g13)
    c: Equal(g18,g17)
    c: Equal(g17,g16)
    c: Horizontal(g8)
    c: Horizontal(g4)
    c: Horizontal(g5)
    c: Equal(g19,g20)
    c: Coincident(g21,g19)
    c: PointOnObject(g21,g-3)
    c: Perpendicular(g-3,g21)
    c: Coincident(g22,g20)
    c: PointOnObject(g22,g-3)
    c: Perpendicular(g-3,g22)
    c: Equal(g21,g22)
    c: Diameter(g19) = 16.5
    c: PointOnObject(g23,g-3)
    c: Coincident(g24,g23)
    c: Equal(g24,g19)
    c: Coincident(g25,g19)
    c: Coincident(g25,g20)
    c: Coincident(g26,g20)
    c: Coincident(g26,g24)
    c: Equal(g25,g26)
    c: Equal(g23,g21)
FEATURE [PartDesign::Pocket] Pocket020
  BaseFeature = -> Pad021
  Direction = (0,1,2e-16)
  Length = 5
  Length2 = 5
  Placement = pos=(0,0,0) rot=(1,0,0;1.5708rad)
  Profile = -> Sketch044
  ReferenceAxis = -> Sketch044 [N_Axis]
  Refine = true
  Type = 1
FEATURE [Sketcher::SketchObject] Sketch046  label="sk_mount_plate003"
  AttachmentOffset = pos=(0,14,0) rot=(0,0,1;0rad)
  FullyConstrained = true
  MapMode = 5
  Placement = pos=(0,-3.1e-15,14) rot=(1,0,0;1.5708rad)
  Support = -> [XZ_Plane010]
  sketch-geometry (14):
    g0: Circle CenterX=-28 CenterY=0 CenterZ=0 NormalX=0 NormalY=0 NormalZ=1 AngleXU=0 Radius=3
    g1: Circle CenterX=28 CenterY=0 CenterZ=0 NormalX=0 NormalY=0 NormalZ=1 AngleXU=0 Radius=3
    g2: Circle CenterX=-50 CenterY=0 CenterZ=0 NormalX=0 NormalY=0 NormalZ=1 AngleXU=0 Radius=5
    g3: Circle CenterX=50 CenterY=0 CenterZ=0 NormalX=0 NormalY=0 NormalZ=1 AngleXU=0 Radius=5
    g4: LineSegment StartX=-50 StartY=0 StartZ=0 EndX=50 EndY=0 EndZ=0
    g5: ArcOfCircle CenterX=1.69e-14 CenterY=-69 CenterZ=0 NormalX=0 NormalY=0 NormalZ=1 AngleXU=0 Radius=100 StartAngle=1.21654 EndAngle=1.92505
    g6: ArcOfCircle CenterX=106.026 CenterY=217.668 CenterZ=0 NormalX=0 NormalY=0 NormalZ=1 AngleXU=0 Radius=205.647 StartAngle=4.35814 EndAngle=4.64413
    g7: GeomPoint X=0 Y=31 Z=0
    g8: LineSegment StartX=28 StartY=0 StartZ=0 EndX=28 EndY=27 EndZ=0
    g9: LineSegment StartX=50 StartY=0 StartZ=0 EndX=50 EndY=19.8 EndZ=0
    g10: ArcOfCircle CenterX=-106.026 CenterY=217.668 CenterZ=0 NormalX=0 NormalY=0 NormalZ=1 AngleXU=0 Radius=205.647 StartAngle=4.78065 EndAngle=5.06664
    g11: LineSegment StartX=-50 StartY=0 StartZ=0 EndX=-50 EndY=19.8 EndZ=0
    g12: LineSegment StartX=-92 StartY=12.5 StartZ=0 EndX=-92 EndY=0 EndZ=0
    g13: LineSegment StartX=92 StartY=12.5 StartZ=0 EndX=92 EndY=0 EndZ=0
  constraints (39):
    c: DistanceX(g0,g1) = 56  'mount_holes_distance'
    c: Symmetric(g0,g1,g-2)
    c: Equal(g0,g1)
    c: Diameter(g0) = 6  'mount_holes_diameter'
    c: Equal(g2,g3)
    c: Diameter(g2) = 10  'motor_mount_holes_diameter'
    c: Symmetric(g2,g3,g-2)
    c: Coincident(g4,g2)
    c: Coincident(g4,g3)
    c: PointOnObject(g0,g4)
    c: PointOnObject(g-1,g4)
    c: Symmetric(g5,g5,g-2)
    c: Coincident(g6,g5)
    c: PointOnObject(g7,g5)
    c: PointOnObject(g7,g-2)
    c: DistanceY(g-1,g7) = 31
    c: Coincident(g8,g1)
    c: PointOnObject(g8,g5)
    c: Vertical(g8)
    c: Coincident(g9,g3)
    c: PointOnObject(g9,g6)
    c: Vertical(g9)
    c: DistanceY(g1,g8) = 27
    c: DistanceX(g2,g3) = 100
    c: DistanceY(g9,g9) = 19.8
    c: Coincident(g11,g2)
    c: PointOnObject(g11,g10)
    c: Vertical(g11)
    c: DistanceY(g11,g11) = 19.8
    c: Symmetric(g6,g10,g-2)
    c: Coincident(g12,g10)
    c: PointOnObject(g12,g-1)
    c: Vertical(g12)
    c: DistanceY(g12,g12) = 12.5
    c: DistanceX(g12,g-1) = 92
    c: Tangent(g10,g5) = 1.5708
    c: Coincident(g13,g6)
    c: PointOnObject(g13,g-1)
    c: Vertical(g13)
FEATURE [Sketcher::SketchObject] Sketch047
  ExternalGeometry = -> [Sketch046]
  FullyConstrained = false
  MapMode = 5
  Placement = pos=(0,0,0) rot=(1,0,0;1.5708rad)
  Support = -> [XZ_Plane010]
  sketch-geometry (19):
    g0: LineSegment StartX=-74.1374 StartY=12.9048 StartZ=0 EndX=-74.1374 EndY=35.0983 EndZ=0
    g1: LineSegment StartX=86.4714 StartY=40.0983 StartZ=0 EndX=86.4714 EndY=91.2347 EndZ=0
    g2: ArcOfCircle CenterX=-86.4323 CenterY=296.882 CenterZ=0 NormalX=0 NormalY=0 NormalZ=1 AngleXU=0 Radius=205.647 StartAngle=4.7122 EndAngle=4.96674
    g3: ArcOfCircle CenterX=86.4323 CenterY=296.882 CenterZ=0 NormalX=0 NormalY=0 NormalZ=1 AngleXU=0 Radius=205.647 StartAngle=4.45804 EndAngle=4.71258
    g4: LineSegment StartX=-34.689 StartY=97.8508 StartZ=0 EndX=-34.689 EndY=38.7906 EndZ=0
    g5: ArcOfCircle CenterX=-5.9e-15 CenterY=4.06019 CenterZ=0 NormalX=0 NormalY=0 NormalZ=1 AngleXU=0 Radius=100 StartAngle=1.21654 EndAngle=1.92505
    g6: LineSegment StartX=-86.4714 StartY=91.2347 StartZ=0 EndX=-86.4714 EndY=40.0983 EndZ=0
    g7: LineSegment StartX=-81.4714 StartY=35.0983 StartZ=0 EndX=-74.1374 EndY=35.0983 EndZ=0
    g8: LineSegment StartX=81.4714 StartY=35.0983 StartZ=0 EndX=74.1374 EndY=35.0983 EndZ=0
    g9: LineSegment StartX=74.1374 StartY=35.0983 StartZ=0 EndX=74.1374 EndY=12.9048 EndZ=0
    g10: ArcOfCircle CenterX=-81.4714 CenterY=40.0983 CenterZ=0 NormalX=0 NormalY=0 NormalZ=1 AngleXU=0 Radius=5 StartAngle=3.14159 EndAngle=4.71239
    g11: ArcOfCircle CenterX=81.4714 CenterY=40.0983 CenterZ=0 NormalX=0 NormalY=0 NormalZ=1 AngleXU=0 Radius=5 StartAngle=4.71239 EndAngle=6.28319
    g12: Circle CenterX=50 CenterY=14 CenterZ=0 NormalX=0 NormalY=0 NormalZ=1 AngleXU=0 Radius=5
    g13: Circle CenterX=28 CenterY=14 CenterZ=0 NormalX=0 NormalY=0 NormalZ=1 AngleXU=0 Radius=3
    g14: Circle CenterX=-28 CenterY=14 CenterZ=0 NormalX=0 NormalY=0 NormalZ=1 AngleXU=0 Radius=3
    g15: Circle CenterX=-50 CenterY=14 CenterZ=0 NormalX=0 NormalY=0 NormalZ=1 AngleXU=0 Radius=5
    g16: LineSegment StartX=-66.2726 StartY=5.0399 StartZ=0 EndX=66.2726 EndY=5.0399 EndZ=0
    g17: ArcOfCircle CenterX=-66.2726 CenterY=12.9048 CenterZ=0 NormalX=0 NormalY=0 NormalZ=1 AngleXU=0 Radius=7.86486 StartAngle=3.14159 EndAngle=4.71239
    g18: ArcOfCircle CenterX=66.2726 CenterY=12.9048 CenterZ=0 NormalX=0 NormalY=0 NormalZ=1 AngleXU=0 Radius=7.86486 StartAngle=4.71239 EndAngle=6.28319
  constraints (40):
    c: Vertical(g0)
    c: Equal(g2,g-3)
    c: Coincident(g3,g1)
    c: Equal(g3,g-5)
    c: Coincident(g4,g2)
    c: Coincident(g4,g-4)
    c: Vertical(g4)
    c: Symmetric(g2,g3,g-2)
    c: Coincident(g5,g2)
    c: Coincident(g5,g3)
    c: Equal(g5,g-4)
    c: Coincident(g6,g2)
    c: Vertical(g6)
    c: Horizontal(g7)
    c: Coincident(g0,g7)
    c: Symmetric(g2,g1,g-2)
    c: Coincident(g9,g8)
    c: Vertical(g9)
    c: Symmetric(g8,g0,g-2)
    c: Tangent(g6,g10) = -1.5708
    c: Tangent(g7,g10) = -1.5708
    c: Tangent(g8,g11) = 1.5708
    c: Tangent(g1,g11) = -1.5708
    c: Equal(g10,g11)
    c: Horizontal(g8)
    c: Vertical(g1)
    c: Radius(g10) = 5
    c: Coincident(g12,g-9)
    c: Coincident(g13,g-8)
    c: Coincident(g14,g-7)
    c: Coincident(g15,g-6)
    c: Equal(g15,g-6)
    c: Equal(g14,g-7)
    c: Equal(g13,g-8)
    c: Equal(g12,g-9)
    c: Tangent(g0,g17) = 1.5708
    c: Tangent(g16,g17) = -1.5708
    c: Tangent(g9,g18) = 1.5708
    c: Tangent(g16,g18) = -1.5708
    c: Symmetric(g16,g16,g-2)
FEATURE [Sketcher::SketchObject] Sketch045
  AttachmentOffset = pos=(0,0,7) rot=(0,0,1;0rad)
  ExternalGeometry = -> [Sketch047]
  FullyConstrained = false
  MapMode = 5
  Placement = pos=(0,-7,-1.6e-15) rot=(1,0,0;1.5708rad)
  Support = -> [XZ_Plane010]
  sketch-geometry (8):
    g0: ArcOfCircle CenterX=-66.2726 CenterY=40.9447 CenterZ=0 NormalX=0 NormalY=0 NormalZ=1 AngleXU=0 Radius=35.9048 StartAngle=3.41409 EndAngle=4.71239
    g1: LineSegment StartX=-66.2726 StartY=5.0399 StartZ=0 EndX=66.2726 EndY=5.0399 EndZ=0
    g2: ArcOfCircle CenterX=22.0989 CenterY=43.5164 CenterZ=0 NormalX=0 NormalY=0 NormalZ=1 AngleXU=0 Radius=123.559 StartAngle=2.74446 EndAngle=3.24078
    g3: ArcOfCircle CenterX=-86.4323 CenterY=296.882 CenterZ=0 NormalX=0 NormalY=0 NormalZ=1 AngleXU=0 Radius=205.647 StartAngle=4.68607 EndAngle=4.96674
    g4: ArcOfCircle CenterX=1.88e-14 CenterY=4.06019 CenterZ=0 NormalX=0 NormalY=0 NormalZ=1 AngleXU=0 Radius=100 StartAngle=1.21654 EndAngle=1.92505
    g5: ArcOfCircle CenterX=86.4323 CenterY=296.882 CenterZ=0 NormalX=0 NormalY=0 NormalZ=1 AngleXU=0 Radius=205.647 StartAngle=4.45804 EndAngle=4.73871
    g6: ArcOfCircle CenterX=66.2726 CenterY=40.9447 CenterZ=0 NormalX=0 NormalY=0 NormalZ=1 AngleXU=0 Radius=35.9048 StartAngle=4.71239 EndAngle=6.01069
    g7: ArcOfCircle CenterX=-22.0989 CenterY=43.5164 CenterZ=0 NormalX=0 NormalY=0 NormalZ=1 AngleXU=0 Radius=123.559 StartAngle=6.184 EndAngle=6.68032
  constraints (20):
    c: Coincident(g0,g-4)
    c: Coincident(g2,g0)
    c: Coincident(g3,g2)
    c: Equal(g3,g-5)
    c: Coincident(g3,g-6)
    c: Coincident(g4,g3)
    c: Coincident(g4,g-7)
    c: Coincident(g5,g4)
    c: Equal(g4,g-6)
    c: Equal(g-7,g5)
    c: Coincident(g6,g-3)
    c: Coincident(g7,g6)
    c: Equal(g7,g2)
    c: Symmetric(g0,g6,g-2)
    c: Equal(g0,g6)
    c: Coincident(g1,g6)
    c: Symmetric(g2,g5,g-2)
    c: Coincident(g5,g7)
    c: PointOnObject(g-5,g3)
    c: Tangent(g1,g0) = -1.5708
FEATURE [PartDesign::Pad] Pad023
  Direction = (0,-1,2e-16)
  Length = 30
  Length2 = 10
  Placement = pos=(0,0,0) rot=(1,0,0;1.5708rad)
  Profile = -> Sketch045
  ReferenceAxis = -> Sketch045 [N_Axis]
  Refine = true
  Type = 0
FEATURE [Sketcher::SketchObject] Sketch049  label="sk_front_screen_frame001"
  AttachmentOffset = pos=(0,0,4) rot=(0,0,1;0rad)
  FullyConstrained = false
  MapMode = 5
  Placement = pos=(0,-4,-9e-16) rot=(1,0,0;1.5708rad)
  Support = -> [XZ_Plane010]
  expr: Constraints[8] = <<Spreadsheet>>.screen_width + 1
  expr: Constraints[9] = <<Spreadsheet>>.screen_height + 1
  sketch-geometry (4):
    g0: LineSegment StartX=-55.3 StartY=72.381 StartZ=0 EndX=55.3 EndY=72.381 EndZ=0
    g1: LineSegment StartX=55.3 StartY=72.381 StartZ=0 EndX=55.3 EndY=9.781 EndZ=0
    g2: LineSegment StartX=55.3 StartY=9.781 StartZ=0 EndX=-55.3 EndY=9.781 EndZ=0
    g3: LineSegment StartX=-55.3 StartY=9.781 StartZ=0 EndX=-55.3 EndY=72.381 EndZ=0
  constraints (10):
    c: Coincident(g0,g1)
    c: Coincident(g1,g2)
    c: Coincident(g2,g3)
    c: Coincident(g3,g0)
    c: Horizontal(g2)
    c: Vertical(g1)
    c: Vertical(g3)
    c: Symmetric(g0,g0,g-2)
    c: DistanceX(g0,g0) = 110.6
    c: DistanceY(g1,g1) = 62.6
FEATURE [Sketcher::SketchObject] Sketch050
  AttachmentOffset = pos=(0,0,12) rot=(0,0,1;0rad)
  ExternalGeometry = -> [Sketch045]
  FullyConstrained = false
  MapMode = 5
  Placement = pos=(0,-12,-2.7e-15) rot=(1,0,0;1.5708rad)
  Support = -> [XZ_Plane010]
  sketch-geometry (6):
    g0: ArcOfCircle CenterX=-92.732 CenterY=289.086 CenterZ=0 NormalX=0 NormalY=0 NormalZ=1 AngleXU=0 Radius=205.647 StartAngle=4.74438 EndAngle=5.01146
    g1: ArcOfCircle CenterX=6.1e-15 CenterY=-2.12568 CenterZ=0 NormalX=0 NormalY=0 NormalZ=1 AngleXU=0 Radius=100 StartAngle=1.24358 EndAngle=1.89802
    g2: ArcOfCircle CenterX=92.732 CenterY=289.086 CenterZ=0 NormalX=0 NormalY=0 NormalZ=1 AngleXU=0 Radius=205.647 StartAngle=4.41332 EndAngle=4.6804
    g3: ArcOfCircle CenterX=-64.5147 CenterY=22.8565 CenterZ=0 NormalX=0 NormalY=0 NormalZ=1 AngleXU=0 Radius=162.432 StartAngle=6.0522 EndAngle=6.6661
    g4: ArcOfCircle CenterX=44.5748 CenterY=24.3741 CenterZ=0 NormalX=0 NormalY=0 NormalZ=1 AngleXU=0 Radius=143.497 StartAngle=2.71656 EndAngle=3.4147
    g5: LineSegment StartX=-93.6036 StartY=-14.33 StartZ=0 EndX=93.6036 EndY=-14.33 EndZ=0
  constraints (12):
    c: Coincident(g1,g0)
    c: Coincident(g2,g1)
    c: Symmetric(g0,g1,g-2)
    c: Symmetric(g2,g0,g-2)
    c: Equal(g0,g-5)
    c: Equal(g1,g-4)
    c: Equal(g2,g-3)
    c: Coincident(g3,g2)
    c: Coincident(g4,g0)
    c: Coincident(g5,g4)
    c: Coincident(g5,g3)
    c: Symmetric(g3,g4,g-2)
FEATURE [Sketcher::SketchObject] Sketch048
  AttachmentOffset = pos=(0,0,102) rot=(0,0,1;0rad)
  ExternalGeometry = -> [Pad023,Sketch050]
  FullyConstrained = false
  MapMode = 5
  Placement = pos=(102,-2.26e-14,2.26e-14) rot=(0.57735,0.57735,0.57735;2.0944rad)
  Support = -> [YZ_Plane010]
  sketch-geometry (3):
    g0: ArcOfCircle CenterX=-229.984 CenterY=-32.2747 CenterZ=0 NormalX=0 NormalY=0 NormalZ=1 AngleXU=0 Radius=224.967 StartAngle=0.249803 EndAngle=0.558123
    g1: LineSegment StartX=-39.156 StartY=23.34 StartZ=0 EndX=-39.156 EndY=86.8668 EndZ=0
    g2: LineSegment StartX=-39.156 StartY=23.34 StartZ=0 EndX=-12 EndY=23.34 EndZ=0
  constraints (7):
    c: Vertical(g1)
    c: Coincident(g2,g1)
    c: Coincident(g2,g0)
    c: Horizontal(g2)
    c: Coincident(g0,g1)
    c: PointOnObject(g0,g-5)
    c: DistanceY(g-1,g0) = 23.34
FEATURE [PartDesign::Pocket] Pocket022
  BaseFeature = -> Pad023
  Direction = (-1,2e-16,-3e-16)
  Length = 5
  Length2 = 5
  Placement = pos=(0,0,0) rot=(1,0,0;1.5708rad)
  Profile = -> Sketch048
  ReferenceAxis = -> Sketch048 [N_Axis]
  Refine = true
  Type = 1
FEATURE [PartDesign::Pocket] Pocket023
  BaseFeature = -> Pocket022
  Direction = (0,1,-2e-16)
  Length = 5
  Length2 = 5
  Placement = pos=(0,0,0) rot=(1,0,0;1.5708rad)
  Profile = -> Sketch050
  ReferenceAxis = -> Sketch050 [N_Axis]
  Refine = true
  Reversed = true
  Type = 1
FEATURE [PartDesign::Pocket] Pocket024
  BaseFeature = -> Pocket023
  Direction = (0,1,-2e-16)
  Length = 5
  Length2 = 5
  Placement = pos=(0,0,0) rot=(1,0,0;1.5708rad)
  Profile = -> Sketch049
  ReferenceAxis = -> Sketch049 [N_Axis]
  Refine = true
  Reversed = true
  Type = 1
FEATURE [Sketcher::SketchObject] Sketch051  label="sk_front_back_display_cutout001"
  AttachmentOffset = pos=(0,41,7) rot=(0,0,1;0rad)
  FullyConstrained = true
  MapMode = 5
  Placement = pos=(0,-7,41) rot=(1,0,0;1.5708rad)
  Support = -> [XZ_Plane010]
  expr: Constraints[8] = <<Spreadsheet>>.display_width + 1
  expr: Constraints[9] = <<Spreadsheet>>.display_height + 1
  sketch-geometry (4):
    g0: LineSegment StartX=-63.19 StartY=34.77 StartZ=0 EndX=57.11 EndY=34.77 EndZ=0
    g1: LineSegment StartX=57.11 StartY=34.77 StartZ=0 EndX=57.11 EndY=-34.93 EndZ=0
    g2: LineSegment StartX=57.11 StartY=-34.93 StartZ=0 EndX=-63.19 EndY=-34.93 EndZ=0
    g3: LineSegment StartX=-63.19 StartY=-34.93 StartZ=0 EndX=-63.19 EndY=34.77 EndZ=0
  constraints (12):
    c: Coincident(g0,g1)
    c: Coincident(g1,g2)
    c: Coincident(g2,g3)
    c: Coincident(g3,g0)
    c: Horizontal(g0)
    c: Horizontal(g2)
    c: Vertical(g1)
    c: Vertical(g3)
    c: DistanceX(g0,g0) = 120.3
    c: DistanceY(g1,g1) = 69.7
    c: DistanceX(g0,g-1) = 63.19
    c: DistanceY(g-1,g0) = 34.77
FEATURE [PartDesign::Pocket] Pocket025
  BaseFeature = -> Pocket024
  Direction = (0,1,-2e-16)
  Length = 2
  Length2 = 5
  Placement = pos=(0,0,0) rot=(1,0,0;1.5708rad)
  Profile = -> Sketch051
  ReferenceAxis = -> Sketch051 [N_Axis]
  Refine = true
  Reversed = true
  Type = 0
FEATURE [PartDesign::Chamfer] Chamfer001
  Angle = 45
  Base = -> Pocket025 [Edge29,Edge28,Edge31,Edge30]
  BaseFeature = -> Pocket025
  ChamferType = 1
  FlipDirection = false
  Placement = pos=(0,0,0) rot=(1,0,0;1.5708rad)
  Refine = true
  Size = 4
  Size2 = 2
  SupportTransform = false
  UseAllEdges = false
FEATURE [Sketcher::SketchObject] Sketch052
  AttachmentOffset = pos=(0,0,12) rot=(0,0,1;0rad)
  FullyConstrained = false
  MapMode = 5
  Placement = pos=(0,-12,-2.7e-15) rot=(1,0,0;1.5708rad)
  Support = -> [XZ_Plane010]
  sketch-geometry (4):
    g0: Circle CenterX=-81.8947 CenterY=30.682 CenterZ=0 NormalX=0 NormalY=0 NormalZ=1 AngleXU=0 Radius=3
    g1: Circle CenterX=81.8947 CenterY=30.682 CenterZ=0 NormalX=0 NormalY=0 NormalZ=1 AngleXU=0 Radius=3
    g2: Circle CenterX=91.3434 CenterY=51.2529 CenterZ=0 NormalX=0 NormalY=0 NormalZ=1 AngleXU=0 Radius=3
    g3: Circle CenterX=-91.3434 CenterY=51.2529 CenterZ=0 NormalX=0 NormalY=0 NormalZ=1 AngleXU=0 Radius=3
  constraints (6):
    c: Diameter(g0) = 6
    c: Symmetric(g1,g0,g-2)
    c: Equal(g1,g0)
    c: Symmetric(g3,g2,g-2)
    c: Equal(g2,g1)
    c: Equal(g1,g3)
FEATURE [Sketcher::SketchObject] Sketch053
  AttachmentOffset = pos=(0,0,37) rot=(0,0,1;0rad)
  FullyConstrained = false
  MapMode = 5
  Placement = pos=(0,-37,-8.2e-15) rot=(1,0,0;1.5708rad)
  Support = -> [XZ_Plane008]
  sketch-geometry (2):
    g0: Circle CenterX=81.8948 CenterY=30.7174 CenterZ=0 NormalX=0 NormalY=0 NormalZ=1 AngleXU=0 Radius=1.25
    g1: Circle CenterX=91.3464 CenterY=51.207 CenterZ=0 NormalX=0 NormalY=0 NormalZ=1 AngleXU=0 Radius=1.25
  constraints (2):
    c: Diameter(g0) = 2.5
    c: Equal(g1,g0)
FEATURE [PartDesign::Pocket] Pocket027
  BaseFeature = -> Pocket020
  Direction = (0,1,2e-16)
  Length = 5
  Length2 = 5
  Placement = pos=(0,0,0) rot=(1,0,0;1.5708rad)
  Profile = -> Sketch053
  ReferenceAxis = -> Sketch053 [N_Axis]
  Refine = true
  Type = 1
FEATURE [PartDesign::Body] Body008  label="Panel_right"
  Group = -> [Sketch043,Pad021,Sketch044,Pocket020,Sketch053,Pocket027]
  Origin = -> Origin008
  Tip = -> Pocket027
FEATURE [Sketcher::SketchObject] Sketch054
  AttachmentOffset = pos=(0,0,14) rot=(0,0,1;0rad)
  ExternalGeometry = -> [Sketch052]
  FullyConstrained = true
  MapMode = 5
  Placement = pos=(0,-14,-3.1e-15) rot=(1,0,0;1.5708rad)
  Support = -> [XZ_Plane010]
  sketch-geometry (4):
    g0: Circle CenterX=-81.8947 CenterY=30.682 CenterZ=0 NormalX=0 NormalY=0 NormalZ=1 AngleXU=0 Radius=1.25
    g1: Circle CenterX=-91.3434 CenterY=51.2529 CenterZ=0 NormalX=0 NormalY=0 NormalZ=1 AngleXU=0 Radius=1.25
    g2: Circle CenterX=91.3434 CenterY=51.2529 CenterZ=0 NormalX=0 NormalY=0 NormalZ=1 AngleXU=0 Radius=1.25
    g3: Circle CenterX=81.8947 CenterY=30.682 CenterZ=0 NormalX=0 NormalY=0 NormalZ=1 AngleXU=0 Radius=1.25
  constraints (8):
    c: Coincident(g-4,g0)
    c: Coincident(g1,g-3)
    c: Coincident(g2,g-6)
    c: Coincident(g3,g-5)
    c: Equal(g1,g0)
    c: Equal(g1,g3)
    c: Equal(g1,g2)
    c: Diameter(g1) = 2.5
FEATURE [PartDesign::Pocket] Pocket029
  BaseFeature = -> Chamfer001
  Direction = (0,1,-2e-16)
  Length = 5
  Length2 = 5
  Placement = pos=(0,0,0) rot=(1,0,0;1.5708rad)
  Profile = -> Sketch054
  ReferenceAxis = -> Sketch054 [N_Axis]
  Refine = true
  Type = 1
FEATURE [PartDesign::Pocket] Pocket030
  BaseFeature = -> Pocket029
  Direction = (0,1,-2e-16)
  Length = 3
  Length2 = 5
  Placement = pos=(0,0,0) rot=(1,0,0;1.5708rad)
  Profile = -> Sketch052
  ReferenceAxis = -> Sketch052 [N_Axis]
  Refine = true
  Type = 0
FEATURE [PartDesign::Body] Body010
  Group = -> [Sketch045,Sketch046,Sketch047,Pad023,Sketch048,Pocket022,Sketch049,Sketch050,Pocket023,Pocket024,Sketch051,Pocket025,Chamfer001,Sketch052,Sketch054,Pocket029,Pocket030]
  Origin = -> Origin010
  Tip = -> Pocket030
FEATURE [Sketcher::SketchObject] MirroredSketch001
  FullyConstrained = false
  Placement = pos=(0,-37,0) rot=(1,0,0;1.5708rad)
  sketch-geometry (2):
    g0: Circle CenterX=-81.8948 CenterY=30.7174 CenterZ=0 NormalX=0 NormalY=0 NormalZ=1 AngleXU=0 Radius=1.25
    g1: Circle CenterX=-91.3464 CenterY=51.207 CenterZ=0 NormalX=0 NormalY=0 NormalZ=1 AngleXU=0 Radius=1.25
  constraints (2):
    c: Diameter(g0) = 2.5
    c: Equal(g1,g0)
FEATURE [PartDesign::Pocket] Pocket031
  BaseFeature = -> Pad022
  Direction = (0,1,0)
  Length = 5
  Length2 = 5
  Placement = pos=(0,0,0) rot=(1,0,0;1.5708rad)
  Profile = -> MirroredSketch001
  ReferenceAxis = -> MirroredSketch001 [N_Axis]
  Refine = true
  Type = 1
FEATURE [Sketcher::SketchObject] MirroredSketch002
  FullyConstrained = false
  Placement = pos=(0,-7,0) rot=(1,0,0;1.5708rad)
  sketch-geometry (27):
    g0: Circle CenterX=-211.699 CenterY=15.68 CenterZ=0 NormalX=0 NormalY=0 NormalZ=1 AngleXU=0 Radius=7.9
    g1: Circle CenterX=-211.699 CenterY=-9.39693 CenterZ=0 NormalX=0 NormalY=0 NormalZ=1 AngleXU=0 Radius=7.9
    g2: Circle CenterX=-238.467 CenterY=15.68 CenterZ=0 NormalX=0 NormalY=0 NormalZ=1 AngleXU=0 Radius=7.9
    g3: Circle CenterX=-238.467 CenterY=-9.39693 CenterZ=0 NormalX=0 NormalY=0 NormalZ=1 AngleXU=0 Radius=7.9
    g4: LineSegment StartX=-211.699 StartY=15.68 StartZ=0 EndX=-238.467 EndY=15.68 EndZ=0
    g5: LineSegment StartX=-238.467 StartY=-9.39693 StartZ=0 EndX=-211.699 EndY=-9.39693 EndZ=0
    g6: Circle CenterX=-211.699 CenterY=40.757 CenterZ=0 NormalX=0 NormalY=0 NormalZ=1 AngleXU=0 Radius=7.9
    g7: Circle CenterX=-238.467 CenterY=40.757 CenterZ=0 NormalX=0 NormalY=0 NormalZ=1 AngleXU=0 Radius=7.9
    g8: LineSegment StartX=-211.699 StartY=40.757 StartZ=0 EndX=-238.467 EndY=40.757 EndZ=0
    g9: LineSegment StartX=-211.699 StartY=-9.39693 StartZ=0 EndX=-211.699 EndY=15.68 EndZ=0
    g10: LineSegment StartX=-211.699 StartY=15.68 StartZ=0 EndX=-211.699 EndY=40.757 EndZ=0
    g11: Circle CenterX=-180.86 CenterY=-25.593 CenterZ=0 NormalX=0 NormalY=0 NormalZ=1 AngleXU=0 Radius=7.9
    g12: Circle CenterX=-177.028 CenterY=-60.1553 CenterZ=0 NormalX=0 NormalY=0 NormalZ=1 AngleXU=0 Radius=7.9
    g13: Circle CenterX=-163.778 CenterY=-92.3061 CenterZ=0 NormalX=0 NormalY=0 NormalZ=1 AngleXU=0 Radius=7.9
    g14: Circle CenterX=-174.975 CenterY=8.67946 CenterZ=0 NormalX=0 NormalY=0 NormalZ=1 AngleXU=0 Radius=7.9
    g15: ArcOfCircle CenterX=-56.5275 CenterY=-29.3007 CenterZ=0 NormalX=0 NormalY=0 NormalZ=1 AngleXU=0 Radius=124.388 StartAngle=2.8313 EndAngle=3.67274
    g16: LineSegment StartX=-174.975 StartY=8.67946 StartZ=0 EndX=-180.86 EndY=-25.593 EndZ=0
    g17: LineSegment StartX=-180.86 StartY=-25.593 StartZ=0 EndX=-177.028 EndY=-60.1553 EndZ=0
    g18: LineSegment StartX=-177.028 StartY=-60.1553 StartZ=0 EndX=-163.778 EndY=-92.3061 EndZ=0
    g19: Circle CenterX=-116.789 CenterY=72.7511 CenterZ=0 NormalX=0 NormalY=0 NormalZ=1 AngleXU=0 Radius=8.25
    g20: Circle CenterX=-146.797 CenterY=68.9164 CenterZ=0 NormalX=0 NormalY=0 NormalZ=1 AngleXU=0 Radius=8.25
    g21: LineSegment StartX=-116.789 StartY=72.7511 StartZ=0 EndX=-118.2 EndY=89.7647 EndZ=0
    g22: LineSegment StartX=-146.797 StartY=68.9164 StartZ=0 EndX=-149.709 EndY=85.7383 EndZ=0
    g23: LineSegment StartX=-184.477 StartY=77.9208 StartZ=0 EndX=-176.436 EndY=62.8607 EndZ=0
    g24: Circle CenterX=-176.436 CenterY=62.8607 CenterZ=0 NormalX=0 NormalY=0 NormalZ=1 AngleXU=0 Radius=8.25
    g25: LineSegment StartX=-116.789 StartY=72.7511 StartZ=0 EndX=-146.797 EndY=68.9164 EndZ=0
    g26: LineSegment StartX=-146.797 StartY=68.9164 StartZ=0 EndX=-176.436 EndY=62.8607 EndZ=0
  constraints (51):
    c: Diameter(g0) = 15.8
    c: Coincident(g4,g0)
    c: Coincident(g4,g2)
    c: Coincident(g5,g3)
    c: Coincident(g5,g1)
    c: Equal(g5,g4)
    c: Coincident(g8,g6)
    c: Coincident(g8,g7)
    c: Equal(g8,g5)
    c: Equal(g6,g0)
    c: Equal(g0,g1)
    c: Equal(g1,g3)
    c: Equal(g3,g2)
    c: Equal(g2,g7)
    c: Coincident(g9,g1)
    c: Coincident(g9,g0)
    c: Coincident(g10,g0)
    c: Coincident(g10,g6)
    c: Equal(g9,g10)
    c: Parallel(g9,g10)
    c: Perpendicular(g9,g5)
    c: Equal(g13,g12)
    c: Equal(g12,g11)
    c: Equal(g11,g14)
    c: Coincident(g15,g13)
    c: PointOnObject(g11,g15)
    c: PointOnObject(g12,g15)
    c: Coincident(g16,g14)
    c: Coincident(g16,g11)
    c: Coincident(g17,g11)
    c: Coincident(g17,g12)
    c: Coincident(g18,g12)
    c: Coincident(g18,g13)
    c: Equal(g18,g17)
    c: Equal(g17,g16)
    c: Horizontal(g8)
    c: Horizontal(g4)
    c: Horizontal(g5)
    c: Equal(g19,g20)
    c: Coincident(g21,g19)
    c: Coincident(g22,g20)
    c: Equal(g21,g22)
    c: Diameter(g19) = 16.5
    c: Coincident(g24,g23)
    c: Equal(g24,g19)
    c: Coincident(g25,g19)
    c: Coincident(g25,g20)
    c: Coincident(g26,g20)
    c: Coincident(g26,g24)
    c: Equal(g25,g26)
    c: Equal(g23,g21)
FEATURE [PartDesign::Pocket] Pocket032
  BaseFeature = -> Pocket031
  Direction = (0,1,0)
  Length = 5
  Length2 = 5
  Placement = pos=(0,0,0) rot=(1,0,0;1.5708rad)
  Profile = -> MirroredSketch002
  ReferenceAxis = -> MirroredSketch002 [N_Axis]
  Refine = true
  Type = 1
FEATURE [PartDesign::Body] Body009  label="Panel_left"
  Group = -> [MirroredSketch,Pad022,MirroredSketch001,Pocket031,MirroredSketch002,Pocket032]
  Origin = -> Origin009
  Tip = -> Pocket032
FEATURE [Sketcher::SketchObject] Sketch055  label="sk_front_back_display_cutout002"
  AttachmentOffset = pos=(6,41,7) rot=(0,0,1;0rad)
  FullyConstrained = true
  MapMode = 5
  Placement = pos=(6,-7,41) rot=(1,0,0;1.5708rad)
  Support = -> [XZ_Plane007]
  expr: Constraints[8] = <<Spreadsheet>>.display_width + 1
  expr: Constraints[9] = <<Spreadsheet>>.display_height + 1
  sketch-geometry (4):
    g0: LineSegment StartX=-63.19 StartY=34.77 StartZ=0 EndX=57.11 EndY=34.77 EndZ=0
    g1: LineSegment StartX=57.11 StartY=34.77 StartZ=0 EndX=57.11 EndY=-34.93 EndZ=0
    g2: LineSegment StartX=57.11 StartY=-34.93 StartZ=0 EndX=-63.19 EndY=-34.93 EndZ=0
    g3: LineSegment StartX=-63.19 StartY=-34.93 StartZ=0 EndX=-63.19 EndY=34.77 EndZ=0
  constraints (12):
    c: Coincident(g0,g1)
    c: Coincident(g1,g2)
    c: Coincident(g2,g3)
    c: Coincident(g3,g0)
    c: Horizontal(g0)
    c: Horizontal(g2)
    c: Vertical(g1)
    c: Vertical(g3)
    c: DistanceX(g0,g0) = 120.3
    c: DistanceY(g1,g1) = 69.7
    c: DistanceX(g0,g-1) = 63.19
    c: DistanceY(g-1,g0) = 34.77
FEATURE [PartDesign::Pocket] Pocket033
  BaseFeature = -> Pocket019
  Direction = (0,1,2e-16)
  Length = 2
  Length2 = 5
  Placement = pos=(0,0,0) rot=(1,0,0;1.5708rad)
  Profile = -> Sketch055
  ReferenceAxis = -> Sketch055 [N_Axis]
  Refine = true
  Type = 0
FEATURE [PartDesign::Body] Body007
  Group = -> [Sketch037,Sketch036,Sketch038,Pad019,Pad020,Sketch041,Pocket019,Sketch055,Pocket033]
  Origin = -> Origin007
  Tip = -> Pocket033
FEATURE [Mesh::Feature] Mesh  label="front (Meshed)"
FEATURE [Mesh::Feature] Mesh001  label="Body (Meshed)"
